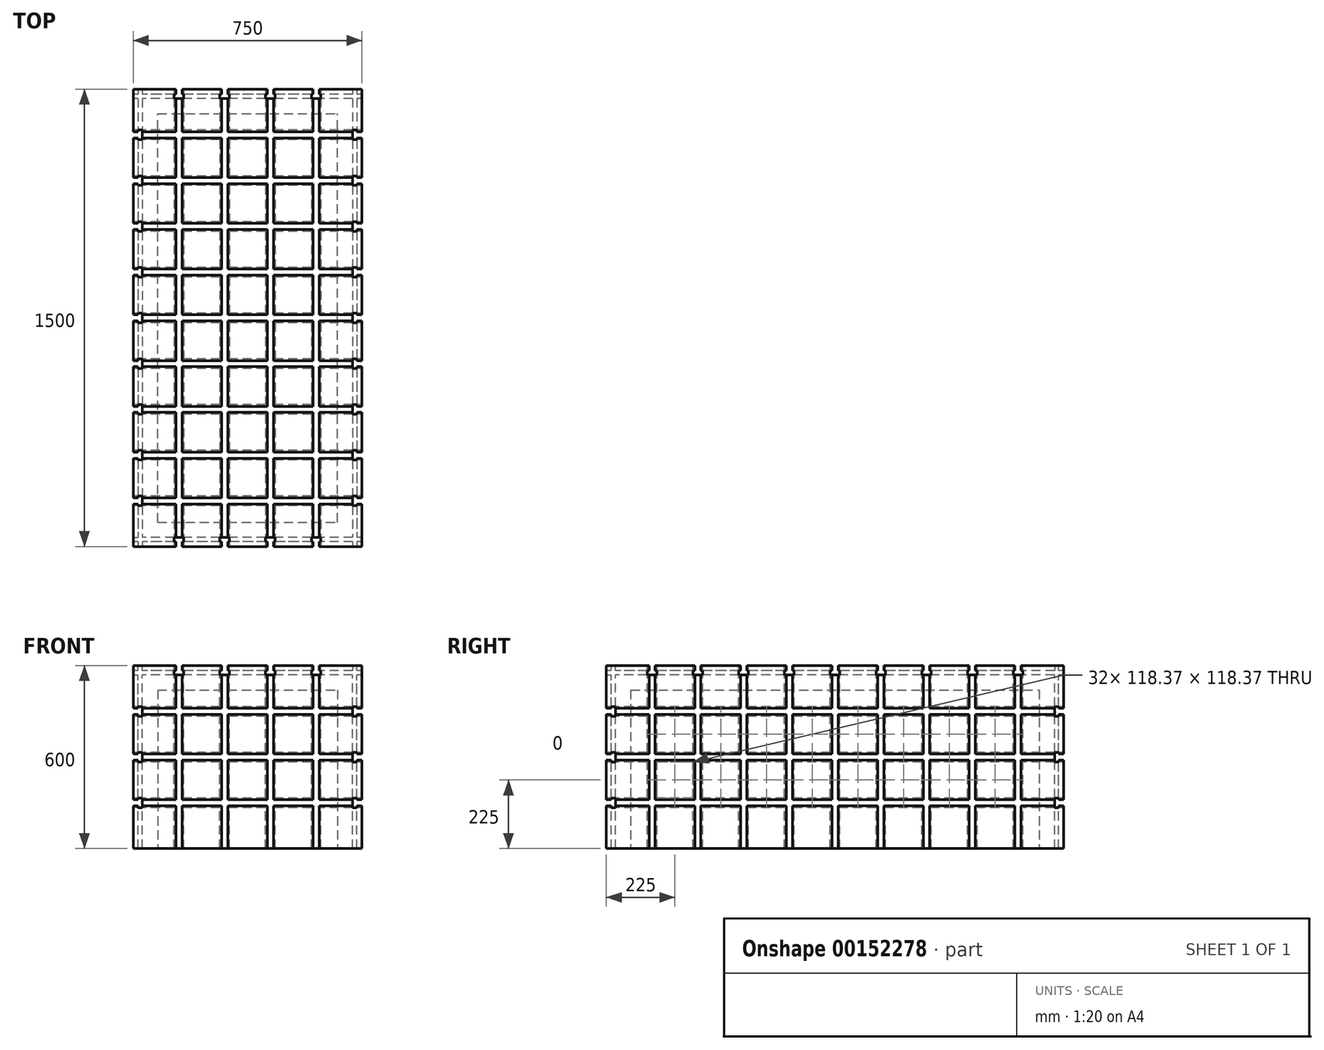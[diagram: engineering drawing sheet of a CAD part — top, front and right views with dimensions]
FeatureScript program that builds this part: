
annotation { "Feature Type Name" : "Feature", "Feature Type Description" : "" }
export const myFeature = defineFeature(function(context is Context, id is Id, definition is map)
    precondition{}
    {
        {
            var Q0;
            Q0=qCreatedBy(makeId("Top.planeOp"),FACE);
            var sketch = newSketch(context, id + "F0", { "sketchPlane" : qUnion([Q0])});
            skLineSegment(sketch, "E0.bottom", {"start": v(-375, 750) * mm, "end": v(375, 750) * mm});
            skLineSegment(sketch, "E0.top", {"start": v(-375, -750) * mm, "end": v(375, -750) * mm});
            skLineSegment(sketch, "E0.left", {"start": v(-375, 750) * mm, "end": v(-375, -750) * mm});
            skLineSegment(sketch, "E0.right", {"start": v(375, 750) * mm, "end": v(375, -750) * mm});
            skPoint(sketch, "E0.middle", {"position": v(0, 0) * mm});
            skSolve(sketch);
        }
        {
            var Q0;
            Q0 = qSketchRegion(id + "F0", true);
            extrude(context, id + "F1", {"entities" : qUnion([Q0]), "oppositeDirection" : true, "depth" : 600 * mm});
        }
        {
            var Q0;
            Q0=makeQuery(id+"F1.opExtrude","SWEPT_FACE",FACE,{"disambiguationData":[OSD([sQuery(id+"F0.wireOp",EDGE,"E0.top")])]});
            var sketch = newSketch(context, id + "F2", { "sketchPlane" : qUnion([Q0])});
            skLineSegment(sketch, "E1", {"start": v(0, 0) * mm, "end": v(0, -600) * mm, "construction": true});
            skLineSegment(sketch, "E2", {"start": v(-375, -300) * mm, "end": v(375, -300) * mm, "construction": true});
            skLineSegment(sketch, "E3", {"start": v(-225, 0) * mm, "end": v(-225, -600) * mm, "construction": true});
            skLineSegment(sketch, "E4", {"start": v(-75, 0) * mm, "end": v(-75, -600) * mm, "construction": true});
            skLineSegment(sketch, "E5.MirrorCS", {"start": v(75, 0) * mm, "end": v(75, -600) * mm, "construction": true});
            skLineSegment(sketch, "E6.MirrorCS", {"start": v(225, 0) * mm, "end": v(225, -600) * mm, "construction": true});
            skLineSegment(sketch, "E7", {"start": v(-375, -150) * mm, "end": v(375, -150) * mm, "construction": true});
            skLineSegment(sketch, "E8.MirrorCS", {"start": v(-375, -450) * mm, "end": v(375, -450) * mm, "construction": true});
            skLineSegment(sketch, "E9", {"start": v(-235, 0) * mm, "end": v(-235, -16.46) * mm});
            skLineSegment(sketch, "E10", {"start": v(-235, -16.46) * mm, "end": v(-240.81, -16.46) * mm});
            skLineSegment(sketch, "E11", {"start": v(-240.81, -16.46) * mm, "end": v(-240.81, -30.16) * mm});
            skLineSegment(sketch, "E12", {"start": v(-240.81, -30.16) * mm, "end": v(-225, -30.16) * mm});
            skLineSegment(sketch, "E13", {"start": v(-235, 0) * mm, "end": v(-235, 10) * mm});
            skLineSegment(sketch, "E14", {"start": v(-235, 10) * mm, "end": v(-225, 10) * mm});
            skLineSegment(sketch, "E15.MirrorCS", {"start": v(-215, -16.46) * mm, "end": v(-209.18, -16.46) * mm});
            skLineSegment(sketch, "E16.MirrorCS", {"start": v(-215, 0) * mm, "end": v(-215, -16.46) * mm});
            skLineSegment(sketch, "E17.MirrorCS", {"start": v(-209.18, -16.46) * mm, "end": v(-209.18, -30.16) * mm});
            skLineSegment(sketch, "E18.MirrorCS", {"start": v(-215, 10) * mm, "end": v(-225, 10) * mm});
            skLineSegment(sketch, "E19.MirrorCS", {"start": v(-209.18, -30.16) * mm, "end": v(-225, -30.16) * mm});
            skLineSegment(sketch, "E20.MirrorCS", {"start": v(-215, 0) * mm, "end": v(-215, 10) * mm});
            skLineSegment(sketch, "E21.1.0.0", {"start": v(-59.18, -16.46) * mm, "end": v(-59.18, -30.16) * mm});
            skLineSegment(sketch, "E21.1.0.1", {"start": v(-59.18, -30.16) * mm, "end": v(-75, -30.16) * mm});
            skLineSegment(sketch, "E21.1.0.2", {"start": v(-85, 0) * mm, "end": v(-85, 10) * mm});
            skLineSegment(sketch, "E21.1.0.3", {"start": v(-65, 0) * mm, "end": v(-65, 10) * mm});
            skLineSegment(sketch, "E21.1.0.4", {"start": v(-65, 10) * mm, "end": v(-75, 10) * mm});
            skLineSegment(sketch, "E21.1.0.5", {"start": v(-90.81, -30.16) * mm, "end": v(-75, -30.16) * mm});
            skLineSegment(sketch, "E21.1.0.6", {"start": v(-90.81, -16.46) * mm, "end": v(-90.81, -30.16) * mm});
            skLineSegment(sketch, "E21.1.0.7", {"start": v(-85, 10) * mm, "end": v(-75, 10) * mm});
            skLineSegment(sketch, "E21.1.0.8", {"start": v(-85, 0) * mm, "end": v(-85, -16.46) * mm});
            skLineSegment(sketch, "E21.1.0.9", {"start": v(-65, 0) * mm, "end": v(-65, -16.46) * mm});
            skLineSegment(sketch, "E21.1.0.10", {"start": v(-85, -16.46) * mm, "end": v(-90.81, -16.46) * mm});
            skLineSegment(sketch, "E21.1.0.11", {"start": v(-65, -16.46) * mm, "end": v(-59.18, -16.46) * mm});
            skLineSegment(sketch, "E21.2.0.0", {"start": v(90.82, -16.46) * mm, "end": v(90.82, -30.16) * mm});
            skLineSegment(sketch, "E21.2.0.1", {"start": v(90.82, -30.16) * mm, "end": v(75, -30.16) * mm});
            skLineSegment(sketch, "E21.2.0.2", {"start": v(65, 0) * mm, "end": v(65, 10) * mm});
            skLineSegment(sketch, "E21.2.0.3", {"start": v(85, 0) * mm, "end": v(85, 10) * mm});
            skLineSegment(sketch, "E21.2.0.4", {"start": v(85, 10) * mm, "end": v(75, 10) * mm});
            skLineSegment(sketch, "E21.2.0.5", {"start": v(59.19, -30.16) * mm, "end": v(75, -30.16) * mm});
            skLineSegment(sketch, "E21.2.0.6", {"start": v(59.19, -16.46) * mm, "end": v(59.19, -30.16) * mm});
            skLineSegment(sketch, "E21.2.0.7", {"start": v(65, 10) * mm, "end": v(75, 10) * mm});
            skLineSegment(sketch, "E21.2.0.8", {"start": v(65, 0) * mm, "end": v(65, -16.46) * mm});
            skLineSegment(sketch, "E21.2.0.9", {"start": v(85, 0) * mm, "end": v(85, -16.46) * mm});
            skLineSegment(sketch, "E21.2.0.10", {"start": v(65, -16.46) * mm, "end": v(59.19, -16.46) * mm});
            skLineSegment(sketch, "E21.2.0.11", {"start": v(85, -16.46) * mm, "end": v(90.82, -16.46) * mm});
            skLineSegment(sketch, "E21.3.0.0", {"start": v(240.82, -16.46) * mm, "end": v(240.82, -30.16) * mm});
            skLineSegment(sketch, "E21.3.0.1", {"start": v(240.82, -30.16) * mm, "end": v(225, -30.16) * mm});
            skLineSegment(sketch, "E21.3.0.2", {"start": v(215, 0) * mm, "end": v(215, 10) * mm});
            skLineSegment(sketch, "E21.3.0.3", {"start": v(235, 0) * mm, "end": v(235, 10) * mm});
            skLineSegment(sketch, "E21.3.0.4", {"start": v(235, 10) * mm, "end": v(225, 10) * mm});
            skLineSegment(sketch, "E21.3.0.5", {"start": v(209.19, -30.16) * mm, "end": v(225, -30.16) * mm});
            skLineSegment(sketch, "E21.3.0.6", {"start": v(209.19, -16.46) * mm, "end": v(209.19, -30.16) * mm});
            skLineSegment(sketch, "E21.3.0.7", {"start": v(215, 10) * mm, "end": v(225, 10) * mm});
            skLineSegment(sketch, "E21.3.0.8", {"start": v(215, 0) * mm, "end": v(215, -16.46) * mm});
            skLineSegment(sketch, "E21.3.0.9", {"start": v(235, 0) * mm, "end": v(235, -16.46) * mm});
            skLineSegment(sketch, "E21.3.0.10", {"start": v(215, -16.46) * mm, "end": v(209.19, -16.46) * mm});
            skLineSegment(sketch, "E21.3.0.11", {"start": v(235, -16.46) * mm, "end": v(240.81, -16.46) * mm});
            skLineSegment(sketch, "E21.direction1", {"start": v(-240.81, -30.16) * mm, "end": v(-90.81, -30.16) * mm, "construction": true});
            skLineSegment(sketch, "E22", {"start": v(-375, -160) * mm, "end": v(-358.54, -160) * mm});
            skLineSegment(sketch, "E23", {"start": v(-358.54, -160) * mm, "end": v(-358.54, -165.82) * mm});
            skLineSegment(sketch, "E24", {"start": v(-358.54, -165.82) * mm, "end": v(-344.84, -165.82) * mm});
            skLineSegment(sketch, "E25", {"start": v(-344.84, -165.82) * mm, "end": v(-344.84, -150) * mm});
            skLineSegment(sketch, "E26", {"start": v(-375, -160) * mm, "end": v(-385, -160) * mm});
            skLineSegment(sketch, "E27", {"start": v(-385, -160) * mm, "end": v(-385, -150) * mm});
            skLineSegment(sketch, "E28.MirrorCS", {"start": v(-358.54, -134.18) * mm, "end": v(-344.84, -134.18) * mm});
            skLineSegment(sketch, "E29.MirrorCS", {"start": v(-358.54, -140) * mm, "end": v(-358.54, -134.18) * mm});
            skLineSegment(sketch, "E30.MirrorCS", {"start": v(-375, -140) * mm, "end": v(-358.54, -140) * mm});
            skLineSegment(sketch, "E31.MirrorCS", {"start": v(-344.84, -134.18) * mm, "end": v(-344.84, -150) * mm});
            skLineSegment(sketch, "E32.MirrorCS", {"start": v(-375, -140) * mm, "end": v(-385, -140) * mm});
            skLineSegment(sketch, "E33.MirrorCS", {"start": v(-385, -140) * mm, "end": v(-385, -150) * mm});
            skLineSegment(sketch, "E34.0.1.0", {"start": v(-375, -310) * mm, "end": v(-358.54, -310) * mm});
            skLineSegment(sketch, "E34.0.1.1", {"start": v(-375, -290) * mm, "end": v(-358.54, -290) * mm});
            skLineSegment(sketch, "E34.0.1.2", {"start": v(-344.84, -284.18) * mm, "end": v(-344.84, -300) * mm});
            skLineSegment(sketch, "E34.0.1.3", {"start": v(-358.54, -290) * mm, "end": v(-358.54, -284.18) * mm});
            skLineSegment(sketch, "E34.0.1.4", {"start": v(-358.54, -284.18) * mm, "end": v(-344.84, -284.18) * mm});
            skLineSegment(sketch, "E34.0.1.5", {"start": v(-385, -310) * mm, "end": v(-385, -300) * mm});
            skLineSegment(sketch, "E34.0.1.6", {"start": v(-344.84, -315.82) * mm, "end": v(-344.84, -300) * mm});
            skLineSegment(sketch, "E34.0.1.7", {"start": v(-375, -310) * mm, "end": v(-385, -310) * mm});
            skLineSegment(sketch, "E34.0.1.8", {"start": v(-385, -290) * mm, "end": v(-385, -300) * mm});
            skLineSegment(sketch, "E34.0.1.9", {"start": v(-358.54, -315.82) * mm, "end": v(-344.84, -315.82) * mm});
            skLineSegment(sketch, "E34.0.1.10", {"start": v(-375, -290) * mm, "end": v(-385, -290) * mm});
            skLineSegment(sketch, "E34.0.1.11", {"start": v(-358.54, -310) * mm, "end": v(-358.54, -315.82) * mm});
            skLineSegment(sketch, "E34.0.2.0", {"start": v(-375, -460) * mm, "end": v(-358.54, -460) * mm});
            skLineSegment(sketch, "E34.0.2.1", {"start": v(-375, -440) * mm, "end": v(-358.54, -440) * mm});
            skLineSegment(sketch, "E34.0.2.2", {"start": v(-344.84, -434.18) * mm, "end": v(-344.84, -450) * mm});
            skLineSegment(sketch, "E34.0.2.3", {"start": v(-358.54, -440) * mm, "end": v(-358.54, -434.18) * mm});
            skLineSegment(sketch, "E34.0.2.4", {"start": v(-358.54, -434.19) * mm, "end": v(-344.84, -434.19) * mm});
            skLineSegment(sketch, "E34.0.2.5", {"start": v(-385, -460) * mm, "end": v(-385, -450) * mm});
            skLineSegment(sketch, "E34.0.2.6", {"start": v(-344.84, -465.82) * mm, "end": v(-344.84, -450) * mm});
            skLineSegment(sketch, "E34.0.2.7", {"start": v(-375, -460) * mm, "end": v(-385, -460) * mm});
            skLineSegment(sketch, "E34.0.2.8", {"start": v(-385, -440) * mm, "end": v(-385, -450) * mm});
            skLineSegment(sketch, "E34.0.2.9", {"start": v(-358.54, -465.82) * mm, "end": v(-344.84, -465.82) * mm});
            skLineSegment(sketch, "E34.0.2.10", {"start": v(-375, -440) * mm, "end": v(-385, -440) * mm});
            skLineSegment(sketch, "E34.0.2.11", {"start": v(-358.54, -460) * mm, "end": v(-358.54, -465.82) * mm});
            skLineSegment(sketch, "E34.direction1", {"start": v(-3796.34, -160) * mm, "end": v(-385, -160) * mm, "construction": true});
            skLineSegment(sketch, "E34.direction2", {"start": v(-385, -160) * mm, "end": v(-385, -310) * mm, "construction": true});
            skLineSegment(sketch, "E35.MirrorCS", {"start": v(3796.34, -160) * mm, "end": v(385, -160) * mm, "construction": true});
            skLineSegment(sketch, "E36.MirrorCS", {"start": v(375, -160) * mm, "end": v(385, -160) * mm});
            skLineSegment(sketch, "E37.MirrorCS", {"start": v(385, -160) * mm, "end": v(385, -150) * mm});
            skLineSegment(sketch, "E38.MirrorCS", {"start": v(385, -310) * mm, "end": v(385, -300) * mm});
            skLineSegment(sketch, "E39.MirrorCS", {"start": v(385, -290) * mm, "end": v(385, -300) * mm});
            skLineSegment(sketch, "E40.MirrorCS", {"start": v(358.54, -440) * mm, "end": v(358.54, -434.18) * mm});
            skLineSegment(sketch, "E41.MirrorCS", {"start": v(375, -310) * mm, "end": v(385, -310) * mm});
            skLineSegment(sketch, "E42.MirrorCS", {"start": v(375, -290) * mm, "end": v(385, -290) * mm});
            skLineSegment(sketch, "E43.MirrorCS", {"start": v(375, -140) * mm, "end": v(385, -140) * mm});
            skLineSegment(sketch, "E44.MirrorCS", {"start": v(358.54, -160) * mm, "end": v(358.54, -165.82) * mm});
            skLineSegment(sketch, "E45.MirrorCS", {"start": v(375, -440) * mm, "end": v(358.54, -440) * mm});
            skLineSegment(sketch, "E46.MirrorCS", {"start": v(385, -440) * mm, "end": v(385, -450) * mm});
            skLineSegment(sketch, "E47.MirrorCS", {"start": v(358.54, -165.82) * mm, "end": v(344.84, -165.82) * mm});
            skLineSegment(sketch, "E48.MirrorCS", {"start": v(375, -440) * mm, "end": v(385, -440) * mm});
            skLineSegment(sketch, "E49.MirrorCS", {"start": v(385, -140) * mm, "end": v(385, -150) * mm});
            skLineSegment(sketch, "E50.MirrorCS", {"start": v(375, -160) * mm, "end": v(358.54, -160) * mm});
            skLineSegment(sketch, "E51.MirrorCS", {"start": v(358.54, -434.19) * mm, "end": v(344.84, -434.19) * mm});
            skLineSegment(sketch, "E52.MirrorCS", {"start": v(344.84, -165.82) * mm, "end": v(344.84, -150) * mm});
            skLineSegment(sketch, "E53.MirrorCS", {"start": v(375, -290) * mm, "end": v(358.54, -290) * mm});
            skLineSegment(sketch, "E54.MirrorCS", {"start": v(358.54, -460) * mm, "end": v(358.54, -465.82) * mm});
            skLineSegment(sketch, "E55.MirrorCS", {"start": v(344.84, -434.18) * mm, "end": v(344.84, -450) * mm});
            skLineSegment(sketch, "E56.MirrorCS", {"start": v(358.54, -465.82) * mm, "end": v(344.84, -465.82) * mm});
            skLineSegment(sketch, "E57.MirrorCS", {"start": v(344.84, -134.18) * mm, "end": v(344.84, -150) * mm});
            skLineSegment(sketch, "E58.MirrorCS", {"start": v(344.84, -315.82) * mm, "end": v(344.84, -300) * mm});
            skLineSegment(sketch, "E59.MirrorCS", {"start": v(358.54, -284.18) * mm, "end": v(344.84, -284.18) * mm});
            skLineSegment(sketch, "E60.MirrorCS", {"start": v(375, -140) * mm, "end": v(358.54, -140) * mm});
            skLineSegment(sketch, "E61.MirrorCS", {"start": v(375, -460) * mm, "end": v(358.54, -460) * mm});
            skLineSegment(sketch, "E62.MirrorCS", {"start": v(375, -460) * mm, "end": v(385, -460) * mm});
            skLineSegment(sketch, "E63.MirrorCS", {"start": v(358.54, -290) * mm, "end": v(358.54, -284.18) * mm});
            skLineSegment(sketch, "E64.MirrorCS", {"start": v(344.84, -465.82) * mm, "end": v(344.84, -450) * mm});
            skLineSegment(sketch, "E65.MirrorCS", {"start": v(344.84, -284.18) * mm, "end": v(344.84, -300) * mm});
            skLineSegment(sketch, "E66.MirrorCS", {"start": v(375, -310) * mm, "end": v(358.54, -310) * mm});
            skLineSegment(sketch, "E67.MirrorCS", {"start": v(358.54, -310) * mm, "end": v(358.54, -315.82) * mm});
            skLineSegment(sketch, "E68.MirrorCS", {"start": v(385, -460) * mm, "end": v(385, -450) * mm});
            skLineSegment(sketch, "E69.MirrorCS", {"start": v(358.54, -134.18) * mm, "end": v(344.84, -134.18) * mm});
            skLineSegment(sketch, "E70.MirrorCS", {"start": v(358.54, -140) * mm, "end": v(358.54, -134.18) * mm});
            skLineSegment(sketch, "E71.MirrorCS", {"start": v(358.54, -315.82) * mm, "end": v(344.84, -315.82) * mm});
            skLineSegment(sketch, "E72.MirrorCS", {"start": v(385, -160) * mm, "end": v(385, -310) * mm, "construction": true});
            skSolve(sketch);
        }
        {
            var Q0;
            Q0 = qSketchRegion(id + "F2", true);
            extrude(context, id + "F3", {"entities" : qUnion([Q0]), "operationType" : NewBodyOperationType.REMOVE, "endBound" : BoundingType.THROUGH_ALL, "oppositeDirection" : true, "depth" : 25 * mm});
        }
        {
            var Q0;
            {var subQ1=sQuery(id+"F0.wireOp",EDGE,"E0.left");Q0=makeQuery(id+"F3.boolean.opBoolean","SPLIT",FACE,{"disambiguationData":[TD([makeQuery(id+"F3.opExtrude","SWEPT_FACE",FACE,{"disambiguationData":[OSD([sQuery(id+"F2.wireOp",EDGE,"E34.0.2.0"),sQuery(id+"F2.wireOp",EDGE,"E34.0.2.7")])]})])],"derivedFrom":makeQuery(id+"F1.opExtrude","SWEPT_FACE",FACE,{"disambiguationData":[OSD([subQ1])]})});}
            var sketch = newSketch(context, id + "F4", { "sketchPlane" : qUnion([Q0])});
            skLineSegment(sketch, "E73", {"start": v(-600, 0) * mm, "end": v(-600, -600) * mm, "construction": true});
            skLineSegment(sketch, "E74.1.0.0", {"start": v(-450, 0) * mm, "end": v(-450, -600) * mm, "construction": true});
            skLineSegment(sketch, "E74.2.0.0", {"start": v(-300, 0) * mm, "end": v(-300, -600) * mm, "construction": true});
            skLineSegment(sketch, "E74.3.0.0", {"start": v(-150, 0) * mm, "end": v(-150, -600) * mm, "construction": true});
            skLineSegment(sketch, "E74.4.0.0", {"start": v(0, 0) * mm, "end": v(0, -600) * mm, "construction": true});
            skLineSegment(sketch, "E74.5.0.0", {"start": v(150, 0) * mm, "end": v(150, -600) * mm, "construction": true});
            skLineSegment(sketch, "E74.6.0.0", {"start": v(300, 0) * mm, "end": v(300, -600) * mm, "construction": true});
            skLineSegment(sketch, "E74.7.0.0", {"start": v(450, 0) * mm, "end": v(450, -600) * mm, "construction": true});
            skLineSegment(sketch, "E74.8.0.0", {"start": v(600, 0) * mm, "end": v(600, -600) * mm, "construction": true});
            skLineSegment(sketch, "E74.direction1", {"start": v(-600, -600) * mm, "end": v(-450, -600) * mm, "construction": true});
            skLineSegment(sketch, "E75", {"start": v(-750, -450) * mm, "end": v(750, -450) * mm, "construction": true});
            skLineSegment(sketch, "E76", {"start": v(-610, 0) * mm, "end": v(-610, -16.46) * mm});
            skLineSegment(sketch, "E77", {"start": v(-610, -16.46) * mm, "end": v(-615.81, -16.46) * mm});
            skLineSegment(sketch, "E78", {"start": v(-615.81, -16.46) * mm, "end": v(-615.81, -30.16) * mm});
            skLineSegment(sketch, "E79", {"start": v(-615.81, -30.16) * mm, "end": v(-600, -30.16) * mm});
            skLineSegment(sketch, "E80", {"start": v(-610, 0) * mm, "end": v(-610, 49.87) * mm});
            skLineSegment(sketch, "E81", {"start": v(-610, 49.87) * mm, "end": v(-600, 49.87) * mm});
            skLineSegment(sketch, "E82.MirrorCS", {"start": v(-590, -16.46) * mm, "end": v(-584.18, -16.46) * mm});
            skLineSegment(sketch, "E83.MirrorCS", {"start": v(-590, 0) * mm, "end": v(-590, -16.46) * mm});
            skLineSegment(sketch, "E84.MirrorCS", {"start": v(-584.18, -16.46) * mm, "end": v(-584.18, -30.16) * mm});
            skLineSegment(sketch, "E85.MirrorCS", {"start": v(-584.18, -30.16) * mm, "end": v(-600, -30.16) * mm});
            skLineSegment(sketch, "E86.MirrorCS", {"start": v(-590, 0) * mm, "end": v(-590, 49.87) * mm});
            skLineSegment(sketch, "E87.MirrorCS", {"start": v(-590, 49.87) * mm, "end": v(-600, 49.87) * mm});
            skLineSegment(sketch, "E88.1.0.0", {"start": v(-434.18, -30.16) * mm, "end": v(-450, -30.16) * mm});
            skLineSegment(sketch, "E88.1.0.1", {"start": v(-440, 49.87) * mm, "end": v(-450, 49.87) * mm});
            skLineSegment(sketch, "E88.1.0.2", {"start": v(-465.81, -30.16) * mm, "end": v(-450, -30.16) * mm});
            skLineSegment(sketch, "E88.1.0.3", {"start": v(-460, 49.87) * mm, "end": v(-450, 49.87) * mm});
            skLineSegment(sketch, "E88.1.0.4", {"start": v(-440, 0) * mm, "end": v(-440, -16.46) * mm});
            skLineSegment(sketch, "E88.1.0.5", {"start": v(-434.18, -16.46) * mm, "end": v(-434.18, -30.16) * mm});
            skLineSegment(sketch, "E88.1.0.6", {"start": v(-460, 0) * mm, "end": v(-460, -16.46) * mm});
            skLineSegment(sketch, "E88.1.0.7", {"start": v(-465.81, -16.46) * mm, "end": v(-465.81, -30.16) * mm});
            skLineSegment(sketch, "E88.1.0.8", {"start": v(-440, 0) * mm, "end": v(-440, 49.87) * mm});
            skLineSegment(sketch, "E88.1.0.9", {"start": v(-460, -16.46) * mm, "end": v(-465.81, -16.46) * mm});
            skLineSegment(sketch, "E88.1.0.10", {"start": v(-440, -16.46) * mm, "end": v(-434.18, -16.46) * mm});
            skLineSegment(sketch, "E88.1.0.11", {"start": v(-460, 0) * mm, "end": v(-460, 49.87) * mm});
            skLineSegment(sketch, "E88.2.0.0", {"start": v(-284.18, -30.16) * mm, "end": v(-300, -30.16) * mm});
            skLineSegment(sketch, "E88.2.0.1", {"start": v(-290, 49.87) * mm, "end": v(-300, 49.87) * mm});
            skLineSegment(sketch, "E88.2.0.2", {"start": v(-315.81, -30.16) * mm, "end": v(-300, -30.16) * mm});
            skLineSegment(sketch, "E88.2.0.3", {"start": v(-310, 49.87) * mm, "end": v(-300, 49.87) * mm});
            skLineSegment(sketch, "E88.2.0.4", {"start": v(-290, 0) * mm, "end": v(-290, -16.46) * mm});
            skLineSegment(sketch, "E88.2.0.5", {"start": v(-284.18, -16.46) * mm, "end": v(-284.18, -30.16) * mm});
            skLineSegment(sketch, "E88.2.0.6", {"start": v(-310, 0) * mm, "end": v(-310, -16.46) * mm});
            skLineSegment(sketch, "E88.2.0.7", {"start": v(-315.81, -16.46) * mm, "end": v(-315.81, -30.16) * mm});
            skLineSegment(sketch, "E88.2.0.8", {"start": v(-290, 0) * mm, "end": v(-290, 49.87) * mm});
            skLineSegment(sketch, "E88.2.0.9", {"start": v(-310, -16.46) * mm, "end": v(-315.81, -16.46) * mm});
            skLineSegment(sketch, "E88.2.0.10", {"start": v(-290, -16.46) * mm, "end": v(-284.18, -16.46) * mm});
            skLineSegment(sketch, "E88.2.0.11", {"start": v(-310, 0) * mm, "end": v(-310, 49.87) * mm});
            skLineSegment(sketch, "E88.3.0.0", {"start": v(-134.18, -30.16) * mm, "end": v(-150, -30.16) * mm});
            skLineSegment(sketch, "E88.3.0.1", {"start": v(-140, 49.87) * mm, "end": v(-150, 49.87) * mm});
            skLineSegment(sketch, "E88.3.0.2", {"start": v(-165.81, -30.16) * mm, "end": v(-150, -30.16) * mm});
            skLineSegment(sketch, "E88.3.0.3", {"start": v(-160, 49.87) * mm, "end": v(-150, 49.87) * mm});
            skLineSegment(sketch, "E88.3.0.4", {"start": v(-140, 0) * mm, "end": v(-140, -16.46) * mm});
            skLineSegment(sketch, "E88.3.0.5", {"start": v(-134.18, -16.46) * mm, "end": v(-134.18, -30.16) * mm});
            skLineSegment(sketch, "E88.3.0.6", {"start": v(-160, 0) * mm, "end": v(-160, -16.46) * mm});
            skLineSegment(sketch, "E88.3.0.7", {"start": v(-165.81, -16.46) * mm, "end": v(-165.81, -30.16) * mm});
            skLineSegment(sketch, "E88.3.0.8", {"start": v(-140, 0) * mm, "end": v(-140, 49.87) * mm});
            skLineSegment(sketch, "E88.3.0.9", {"start": v(-160, -16.46) * mm, "end": v(-165.81, -16.46) * mm});
            skLineSegment(sketch, "E88.3.0.10", {"start": v(-140, -16.46) * mm, "end": v(-134.18, -16.46) * mm});
            skLineSegment(sketch, "E88.3.0.11", {"start": v(-160, 0) * mm, "end": v(-160, 49.87) * mm});
            skLineSegment(sketch, "E88.4.0.0", {"start": v(15.82, -30.16) * mm, "end": v(0, -30.16) * mm});
            skLineSegment(sketch, "E88.4.0.1", {"start": v(10, 49.87) * mm, "end": v(0, 49.87) * mm});
            skLineSegment(sketch, "E88.4.0.2", {"start": v(-15.81, -30.16) * mm, "end": v(0, -30.16) * mm});
            skLineSegment(sketch, "E88.4.0.3", {"start": v(-10, 49.87) * mm, "end": v(0, 49.87) * mm});
            skLineSegment(sketch, "E88.4.0.4", {"start": v(10, 0) * mm, "end": v(10, -16.46) * mm});
            skLineSegment(sketch, "E88.4.0.5", {"start": v(15.82, -16.46) * mm, "end": v(15.82, -30.16) * mm});
            skLineSegment(sketch, "E88.4.0.6", {"start": v(-10, 0) * mm, "end": v(-10, -16.46) * mm});
            skLineSegment(sketch, "E88.4.0.7", {"start": v(-15.81, -16.46) * mm, "end": v(-15.81, -30.16) * mm});
            skLineSegment(sketch, "E88.4.0.8", {"start": v(10, 0) * mm, "end": v(10, 49.87) * mm});
            skLineSegment(sketch, "E88.4.0.9", {"start": v(-10, -16.46) * mm, "end": v(-15.81, -16.46) * mm});
            skLineSegment(sketch, "E88.4.0.10", {"start": v(10, -16.46) * mm, "end": v(15.82, -16.46) * mm});
            skLineSegment(sketch, "E88.4.0.11", {"start": v(-10, 0) * mm, "end": v(-10, 49.87) * mm});
            skLineSegment(sketch, "E88.5.0.0", {"start": v(165.82, -30.16) * mm, "end": v(150, -30.16) * mm});
            skLineSegment(sketch, "E88.5.0.1", {"start": v(160, 49.87) * mm, "end": v(150, 49.87) * mm});
            skLineSegment(sketch, "E88.5.0.2", {"start": v(134.19, -30.16) * mm, "end": v(150, -30.16) * mm});
            skLineSegment(sketch, "E88.5.0.3", {"start": v(140, 49.87) * mm, "end": v(150, 49.87) * mm});
            skLineSegment(sketch, "E88.5.0.4", {"start": v(160, 0) * mm, "end": v(160, -16.46) * mm});
            skLineSegment(sketch, "E88.5.0.5", {"start": v(165.82, -16.46) * mm, "end": v(165.82, -30.16) * mm});
            skLineSegment(sketch, "E88.5.0.6", {"start": v(140, 0) * mm, "end": v(140, -16.46) * mm});
            skLineSegment(sketch, "E88.5.0.7", {"start": v(134.19, -16.46) * mm, "end": v(134.19, -30.16) * mm});
            skLineSegment(sketch, "E88.5.0.8", {"start": v(160, 0) * mm, "end": v(160, 49.87) * mm});
            skLineSegment(sketch, "E88.5.0.9", {"start": v(140, -16.46) * mm, "end": v(134.19, -16.46) * mm});
            skLineSegment(sketch, "E88.5.0.10", {"start": v(160, -16.46) * mm, "end": v(165.82, -16.46) * mm});
            skLineSegment(sketch, "E88.5.0.11", {"start": v(140, 0) * mm, "end": v(140, 49.87) * mm});
            skLineSegment(sketch, "E88.6.0.0", {"start": v(315.82, -30.16) * mm, "end": v(300, -30.16) * mm});
            skLineSegment(sketch, "E88.6.0.1", {"start": v(310, 49.87) * mm, "end": v(300, 49.87) * mm});
            skLineSegment(sketch, "E88.6.0.2", {"start": v(284.19, -30.16) * mm, "end": v(300, -30.16) * mm});
            skLineSegment(sketch, "E88.6.0.3", {"start": v(290, 49.87) * mm, "end": v(300, 49.87) * mm});
            skLineSegment(sketch, "E88.6.0.4", {"start": v(310, 0) * mm, "end": v(310, -16.46) * mm});
            skLineSegment(sketch, "E88.6.0.5", {"start": v(315.82, -16.46) * mm, "end": v(315.82, -30.16) * mm});
            skLineSegment(sketch, "E88.6.0.6", {"start": v(290, 0) * mm, "end": v(290, -16.46) * mm});
            skLineSegment(sketch, "E88.6.0.7", {"start": v(284.19, -16.46) * mm, "end": v(284.19, -30.16) * mm});
            skLineSegment(sketch, "E88.6.0.8", {"start": v(310, 0) * mm, "end": v(310, 49.87) * mm});
            skLineSegment(sketch, "E88.6.0.9", {"start": v(290, -16.46) * mm, "end": v(284.19, -16.46) * mm});
            skLineSegment(sketch, "E88.6.0.10", {"start": v(310, -16.46) * mm, "end": v(315.82, -16.46) * mm});
            skLineSegment(sketch, "E88.6.0.11", {"start": v(290, 0) * mm, "end": v(290, 49.87) * mm});
            skLineSegment(sketch, "E88.7.0.0", {"start": v(465.82, -30.16) * mm, "end": v(450, -30.16) * mm});
            skLineSegment(sketch, "E88.7.0.1", {"start": v(460, 49.87) * mm, "end": v(450, 49.87) * mm});
            skLineSegment(sketch, "E88.7.0.2", {"start": v(434.19, -30.16) * mm, "end": v(450, -30.16) * mm});
            skLineSegment(sketch, "E88.7.0.3", {"start": v(440, 49.87) * mm, "end": v(450, 49.87) * mm});
            skLineSegment(sketch, "E88.7.0.4", {"start": v(460, 0) * mm, "end": v(460, -16.46) * mm});
            skLineSegment(sketch, "E88.7.0.5", {"start": v(465.82, -16.46) * mm, "end": v(465.82, -30.16) * mm});
            skLineSegment(sketch, "E88.7.0.6", {"start": v(440, 0) * mm, "end": v(440, -16.46) * mm});
            skLineSegment(sketch, "E88.7.0.7", {"start": v(434.19, -16.46) * mm, "end": v(434.19, -30.16) * mm});
            skLineSegment(sketch, "E88.7.0.8", {"start": v(460, 0) * mm, "end": v(460, 49.87) * mm});
            skLineSegment(sketch, "E88.7.0.9", {"start": v(440, -16.46) * mm, "end": v(434.19, -16.46) * mm});
            skLineSegment(sketch, "E88.7.0.10", {"start": v(460, -16.46) * mm, "end": v(465.82, -16.46) * mm});
            skLineSegment(sketch, "E88.7.0.11", {"start": v(440, 0) * mm, "end": v(440, 49.87) * mm});
            skLineSegment(sketch, "E88.8.0.0", {"start": v(615.82, -30.16) * mm, "end": v(600, -30.16) * mm});
            skLineSegment(sketch, "E88.8.0.1", {"start": v(610, 49.87) * mm, "end": v(600, 49.87) * mm});
            skLineSegment(sketch, "E88.8.0.2", {"start": v(584.19, -30.16) * mm, "end": v(600, -30.16) * mm});
            skLineSegment(sketch, "E88.8.0.3", {"start": v(590, 49.87) * mm, "end": v(600, 49.87) * mm});
            skLineSegment(sketch, "E88.8.0.4", {"start": v(610, 0) * mm, "end": v(610, -16.46) * mm});
            skLineSegment(sketch, "E88.8.0.5", {"start": v(615.82, -16.46) * mm, "end": v(615.82, -30.16) * mm});
            skLineSegment(sketch, "E88.8.0.6", {"start": v(590, 0) * mm, "end": v(590, -16.46) * mm});
            skLineSegment(sketch, "E88.8.0.7", {"start": v(584.19, -16.46) * mm, "end": v(584.19, -30.16) * mm});
            skLineSegment(sketch, "E88.8.0.8", {"start": v(610, 0) * mm, "end": v(610, 49.87) * mm});
            skLineSegment(sketch, "E88.8.0.9", {"start": v(590, -16.46) * mm, "end": v(584.19, -16.46) * mm});
            skLineSegment(sketch, "E88.8.0.10", {"start": v(610, -16.46) * mm, "end": v(615.82, -16.46) * mm});
            skLineSegment(sketch, "E88.8.0.11", {"start": v(590, 0) * mm, "end": v(590, 49.87) * mm});
            skLineSegment(sketch, "E88.direction1", {"start": v(-615.81, -30.16) * mm, "end": v(-465.81, -30.16) * mm, "construction": true});
            skLineSegment(sketch, "E89.0.1.0", {"start": v(-750, -300) * mm, "end": v(750, -300) * mm, "construction": true});
            skLineSegment(sketch, "E89.0.2.0", {"start": v(-750, -150) * mm, "end": v(750, -150) * mm, "construction": true});
            skLineSegment(sketch, "E89.direction1", {"start": v(-750, -450) * mm, "end": v(-725, -450) * mm, "construction": true});
            skLineSegment(sketch, "E89.direction2", {"start": v(-750, -450) * mm, "end": v(-750, -300) * mm, "construction": true});
            skLineSegment(sketch, "E90", {"start": v(-750, -160) * mm, "end": v(-733.54, -160) * mm});
            skLineSegment(sketch, "E91", {"start": v(-733.54, -160) * mm, "end": v(-733.54, -165.82) * mm});
            skLineSegment(sketch, "E92", {"start": v(-733.54, -165.82) * mm, "end": v(-719.84, -165.82) * mm});
            skLineSegment(sketch, "E93", {"start": v(-719.84, -165.82) * mm, "end": v(-719.84, -150) * mm});
            skLineSegment(sketch, "E94", {"start": v(-750, -160) * mm, "end": v(-766.31, -160) * mm});
            skLineSegment(sketch, "E95", {"start": v(-766.31, -160) * mm, "end": v(-766.31, -150) * mm});
            skLineSegment(sketch, "E96.MirrorCS", {"start": v(-733.54, -140) * mm, "end": v(-733.54, -134.18) * mm});
            skLineSegment(sketch, "E97.MirrorCS", {"start": v(-766.31, -140) * mm, "end": v(-766.31, -150) * mm});
            skLineSegment(sketch, "E98.MirrorCS", {"start": v(-750, -140) * mm, "end": v(-766.31, -140) * mm});
            skLineSegment(sketch, "E99.MirrorCS", {"start": v(-733.54, -134.18) * mm, "end": v(-719.84, -134.18) * mm});
            skLineSegment(sketch, "E100.MirrorCS", {"start": v(-719.84, -134.18) * mm, "end": v(-719.84, -150) * mm});
            skLineSegment(sketch, "E101.MirrorCS", {"start": v(-750, -140) * mm, "end": v(-733.54, -140) * mm});
            skLineSegment(sketch, "E102.0.1.0", {"start": v(-719.84, -284.18) * mm, "end": v(-719.84, -300) * mm});
            skLineSegment(sketch, "E102.0.1.1", {"start": v(-766.31, -290) * mm, "end": v(-766.31, -300) * mm});
            skLineSegment(sketch, "E102.0.1.2", {"start": v(-733.54, -315.81) * mm, "end": v(-719.84, -315.81) * mm});
            skLineSegment(sketch, "E102.0.1.3", {"start": v(-750, -290) * mm, "end": v(-766.31, -290) * mm});
            skLineSegment(sketch, "E102.0.1.4", {"start": v(-750, -310) * mm, "end": v(-766.31, -310) * mm});
            skLineSegment(sketch, "E102.0.1.5", {"start": v(-733.54, -284.18) * mm, "end": v(-719.84, -284.18) * mm});
            skLineSegment(sketch, "E102.0.1.6", {"start": v(-766.31, -310) * mm, "end": v(-766.31, -300) * mm});
            skLineSegment(sketch, "E102.0.1.7", {"start": v(-750, -310) * mm, "end": v(-733.54, -310) * mm});
            skLineSegment(sketch, "E102.0.1.8", {"start": v(-719.84, -315.81) * mm, "end": v(-719.84, -300) * mm});
            skLineSegment(sketch, "E102.0.1.9", {"start": v(-750, -290) * mm, "end": v(-733.54, -290) * mm});
            skLineSegment(sketch, "E102.0.1.10", {"start": v(-733.54, -290) * mm, "end": v(-733.54, -284.18) * mm});
            skLineSegment(sketch, "E102.0.1.11", {"start": v(-733.54, -310) * mm, "end": v(-733.54, -315.81) * mm});
            skLineSegment(sketch, "E102.0.2.0", {"start": v(-719.84, -434.19) * mm, "end": v(-719.84, -450) * mm});
            skLineSegment(sketch, "E102.0.2.1", {"start": v(-766.31, -440) * mm, "end": v(-766.31, -450) * mm});
            skLineSegment(sketch, "E102.0.2.2", {"start": v(-733.54, -465.81) * mm, "end": v(-719.84, -465.81) * mm});
            skLineSegment(sketch, "E102.0.2.3", {"start": v(-750, -440) * mm, "end": v(-766.31, -440) * mm});
            skLineSegment(sketch, "E102.0.2.4", {"start": v(-750, -460) * mm, "end": v(-766.31, -460) * mm});
            skLineSegment(sketch, "E102.0.2.5", {"start": v(-733.54, -434.18) * mm, "end": v(-719.84, -434.18) * mm});
            skLineSegment(sketch, "E102.0.2.6", {"start": v(-766.31, -460) * mm, "end": v(-766.31, -450) * mm});
            skLineSegment(sketch, "E102.0.2.7", {"start": v(-750, -460) * mm, "end": v(-733.54, -460) * mm});
            skLineSegment(sketch, "E102.0.2.8", {"start": v(-719.84, -465.82) * mm, "end": v(-719.84, -450) * mm});
            skLineSegment(sketch, "E102.0.2.9", {"start": v(-750, -440) * mm, "end": v(-733.54, -440) * mm});
            skLineSegment(sketch, "E102.0.2.10", {"start": v(-733.54, -440) * mm, "end": v(-733.54, -434.18) * mm});
            skLineSegment(sketch, "E102.0.2.11", {"start": v(-733.54, -460) * mm, "end": v(-733.54, -465.81) * mm});
            skLineSegment(sketch, "E102.direction1", {"start": v(-766.31, -160) * mm, "end": v(-741.31, -160) * mm, "construction": true});
            skLineSegment(sketch, "E102.direction2", {"start": v(-766.31, -160) * mm, "end": v(-766.31, -310) * mm, "construction": true});
            skLineSegment(sketch, "E103.MirrorCS", {"start": v(733.54, -290) * mm, "end": v(733.54, -284.18) * mm});
            skLineSegment(sketch, "E104.MirrorCS", {"start": v(750, -160) * mm, "end": v(766.31, -160) * mm});
            skLineSegment(sketch, "E105.MirrorCS", {"start": v(766.31, -160) * mm, "end": v(741.31, -160) * mm, "construction": true});
            skLineSegment(sketch, "E106.MirrorCS", {"start": v(750, -310) * mm, "end": v(733.54, -310) * mm});
            skLineSegment(sketch, "E107.MirrorCS", {"start": v(733.54, -460) * mm, "end": v(733.54, -465.81) * mm});
            skLineSegment(sketch, "E108.MirrorCS", {"start": v(766.31, -160) * mm, "end": v(766.31, -150) * mm});
            skLineSegment(sketch, "E109.MirrorCS", {"start": v(750, -460) * mm, "end": v(766.31, -460) * mm});
            skLineSegment(sketch, "E110.MirrorCS", {"start": v(750, -310) * mm, "end": v(766.31, -310) * mm});
            skLineSegment(sketch, "E111.MirrorCS", {"start": v(750, -290) * mm, "end": v(766.31, -290) * mm});
            skLineSegment(sketch, "E112.MirrorCS", {"start": v(750, -440) * mm, "end": v(733.54, -440) * mm});
            skLineSegment(sketch, "E113.MirrorCS", {"start": v(733.54, -160) * mm, "end": v(733.54, -165.81) * mm});
            skLineSegment(sketch, "E114.MirrorCS", {"start": v(733.54, -284.18) * mm, "end": v(719.84, -284.18) * mm});
            skLineSegment(sketch, "E115.MirrorCS", {"start": v(750, -440) * mm, "end": v(766.31, -440) * mm});
            skLineSegment(sketch, "E116.MirrorCS", {"start": v(750, -290) * mm, "end": v(733.54, -290) * mm});
            skLineSegment(sketch, "E117.MirrorCS", {"start": v(733.54, -140) * mm, "end": v(733.54, -134.18) * mm});
            skLineSegment(sketch, "E118.MirrorCS", {"start": v(750, -450) * mm, "end": v(725, -450) * mm, "construction": true});
            skLineSegment(sketch, "E119.MirrorCS", {"start": v(750, -140) * mm, "end": v(733.54, -140) * mm});
            skLineSegment(sketch, "E120.MirrorCS", {"start": v(719.84, -315.81) * mm, "end": v(719.84, -300) * mm});
            skLineSegment(sketch, "E121.MirrorCS", {"start": v(719.84, -165.81) * mm, "end": v(719.84, -150) * mm});
            skLineSegment(sketch, "E122.MirrorCS", {"start": v(733.54, -465.81) * mm, "end": v(719.84, -465.81) * mm});
            skLineSegment(sketch, "E123.MirrorCS", {"start": v(750, -160) * mm, "end": v(733.54, -160) * mm});
            skLineSegment(sketch, "E124.MirrorCS", {"start": v(733.54, -310) * mm, "end": v(733.54, -315.81) * mm});
            skLineSegment(sketch, "E125.MirrorCS", {"start": v(719.84, -284.18) * mm, "end": v(719.84, -300) * mm});
            skLineSegment(sketch, "E126.MirrorCS", {"start": v(719.84, -465.81) * mm, "end": v(719.84, -450) * mm});
            skLineSegment(sketch, "E127.MirrorCS", {"start": v(750, -460) * mm, "end": v(733.54, -460) * mm});
            skLineSegment(sketch, "E128.MirrorCS", {"start": v(719.84, -434.18) * mm, "end": v(719.84, -450) * mm});
            skLineSegment(sketch, "E129.MirrorCS", {"start": v(733.54, -440) * mm, "end": v(733.54, -434.18) * mm});
            skLineSegment(sketch, "E130.MirrorCS", {"start": v(766.31, -310) * mm, "end": v(766.31, -300) * mm});
            skLineSegment(sketch, "E131.MirrorCS", {"start": v(750, -140) * mm, "end": v(766.31, -140) * mm});
            skLineSegment(sketch, "E132.MirrorCS", {"start": v(733.54, -165.81) * mm, "end": v(719.84, -165.81) * mm});
            skLineSegment(sketch, "E133.MirrorCS", {"start": v(733.54, -134.18) * mm, "end": v(719.84, -134.18) * mm});
            skLineSegment(sketch, "E134.MirrorCS", {"start": v(733.54, -315.81) * mm, "end": v(719.84, -315.81) * mm});
            skLineSegment(sketch, "E135.MirrorCS", {"start": v(719.84, -134.18) * mm, "end": v(719.84, -150) * mm});
            skLineSegment(sketch, "E136.MirrorCS", {"start": v(766.31, -140) * mm, "end": v(766.31, -150) * mm});
            skLineSegment(sketch, "E137.MirrorCS", {"start": v(766.31, -290) * mm, "end": v(766.31, -300) * mm});
            skLineSegment(sketch, "E138.MirrorCS", {"start": v(733.54, -434.18) * mm, "end": v(719.84, -434.18) * mm});
            skLineSegment(sketch, "E139.MirrorCS", {"start": v(766.31, -460) * mm, "end": v(766.31, -450) * mm});
            skLineSegment(sketch, "E140.MirrorCS", {"start": v(766.31, -440) * mm, "end": v(766.31, -450) * mm});
            skLineSegment(sketch, "E141.MirrorCS", {"start": v(766.31, -160) * mm, "end": v(766.31, -310) * mm, "construction": true});
            skLineSegment(sketch, "E142.MirrorCS", {"start": v(750, -450) * mm, "end": v(750, -300) * mm, "construction": true});
            skSolve(sketch);
        }
        {
            var Q0;
            Q0 = qSketchRegion(id + "F4", true);
            extrude(context, id + "F5", {"entities" : qUnion([Q0]), "operationType" : NewBodyOperationType.REMOVE, "endBound" : BoundingType.THROUGH_ALL, "oppositeDirection" : true, "depth" : 25 * mm});
        }
        {
            var Q0;
            Q0=makeQuery(id+"F5.boolean.opBoolean","MERGE",FACE,{"derivedFrom":[makeQuery(id+"F3.boolean.opBoolean","COPY",FACE,{"derivedFrom":makeQuery(id+"F3.opExtrude","SWEPT_FACE",FACE,{"disambiguationData":[OSD([sQuery(id+"F2.wireOp",EDGE,"E12"),sQuery(id+"F2.wireOp",EDGE,"E19.MirrorCS")])]})}),makeQuery(id+"F3.boolean.opBoolean","COPY",FACE,{"derivedFrom":makeQuery(id+"F3.opExtrude","SWEPT_FACE",FACE,{"disambiguationData":[OSD([sQuery(id+"F2.wireOp",EDGE,"E21.1.0.1"),sQuery(id+"F2.wireOp",EDGE,"E21.1.0.5")])]})}),makeQuery(id+"F3.boolean.opBoolean","COPY",FACE,{"derivedFrom":makeQuery(id+"F3.opExtrude","SWEPT_FACE",FACE,{"disambiguationData":[OSD([sQuery(id+"F2.wireOp",EDGE,"E21.2.0.1"),sQuery(id+"F2.wireOp",EDGE,"E21.2.0.5")])]})}),makeQuery(id+"F3.boolean.opBoolean","COPY",FACE,{"derivedFrom":makeQuery(id+"F3.opExtrude","SWEPT_FACE",FACE,{"disambiguationData":[OSD([sQuery(id+"F2.wireOp",EDGE,"E21.3.0.1"),sQuery(id+"F2.wireOp",EDGE,"E21.3.0.5")])]})}),makeQuery(id+"F5.opExtrude","SWEPT_FACE",FACE,{"disambiguationData":[OSD([sQuery(id+"F4.wireOp",EDGE,"E79"),sQuery(id+"F4.wireOp",EDGE,"E85.MirrorCS")])]}),makeQuery(id+"F5.opExtrude","SWEPT_FACE",FACE,{"disambiguationData":[OSD([sQuery(id+"F4.wireOp",EDGE,"E88.1.0.0"),sQuery(id+"F4.wireOp",EDGE,"E88.1.0.2")])]}),makeQuery(id+"F5.opExtrude","SWEPT_FACE",FACE,{"disambiguationData":[OSD([sQuery(id+"F4.wireOp",EDGE,"E88.2.0.0"),sQuery(id+"F4.wireOp",EDGE,"E88.2.0.2")])]}),makeQuery(id+"F5.opExtrude","SWEPT_FACE",FACE,{"disambiguationData":[OSD([sQuery(id+"F4.wireOp",EDGE,"E88.3.0.0"),sQuery(id+"F4.wireOp",EDGE,"E88.3.0.2")])]}),makeQuery(id+"F5.opExtrude","SWEPT_FACE",FACE,{"disambiguationData":[OSD([sQuery(id+"F4.wireOp",EDGE,"E88.4.0.0"),sQuery(id+"F4.wireOp",EDGE,"E88.4.0.2")])]}),makeQuery(id+"F5.opExtrude","SWEPT_FACE",FACE,{"disambiguationData":[OSD([sQuery(id+"F4.wireOp",EDGE,"E88.5.0.0"),sQuery(id+"F4.wireOp",EDGE,"E88.5.0.2")])]}),makeQuery(id+"F5.opExtrude","SWEPT_FACE",FACE,{"disambiguationData":[OSD([sQuery(id+"F4.wireOp",EDGE,"E88.6.0.0"),sQuery(id+"F4.wireOp",EDGE,"E88.6.0.2")])]}),makeQuery(id+"F5.opExtrude","SWEPT_FACE",FACE,{"disambiguationData":[OSD([sQuery(id+"F4.wireOp",EDGE,"E88.7.0.0"),sQuery(id+"F4.wireOp",EDGE,"E88.7.0.2")])]}),makeQuery(id+"F5.opExtrude","SWEPT_FACE",FACE,{"disambiguationData":[OSD([sQuery(id+"F4.wireOp",EDGE,"E88.8.0.0"),sQuery(id+"F4.wireOp",EDGE,"E88.8.0.2")])]})]});
            var sketch = newSketch(context, id + "F6", { "sketchPlane" : qUnion([Q0])});
            skLineSegment(sketch, "E143", {"start": v(-225, 750) * mm, "end": v(-225, -750) * mm, "construction": true});
            skLineSegment(sketch, "E144.1.0.0", {"start": v(-75, 750) * mm, "end": v(-75, -750) * mm, "construction": true});
            skLineSegment(sketch, "E144.2.0.0", {"start": v(75, 750) * mm, "end": v(75, -750) * mm, "construction": true});
            skLineSegment(sketch, "E144.3.0.0", {"start": v(225, 750) * mm, "end": v(225, -750) * mm, "construction": true});
            skLineSegment(sketch, "E144.direction1", {"start": v(-225, -750) * mm, "end": v(-75, -750) * mm, "construction": true});
            skLineSegment(sketch, "E145", {"start": v(-375, 600) * mm, "end": v(375, 600) * mm, "construction": true});
            skLineSegment(sketch, "E146", {"start": v(-235, 750) * mm, "end": v(-235, 733.54) * mm});
            skLineSegment(sketch, "E147", {"start": v(-235, 733.54) * mm, "end": v(-240.82, 733.54) * mm});
            skLineSegment(sketch, "E148", {"start": v(-240.82, 733.54) * mm, "end": v(-240.82, 719.84) * mm});
            skLineSegment(sketch, "E149", {"start": v(-240.82, 719.84) * mm, "end": v(-225, 719.84) * mm});
            skLineSegment(sketch, "E150", {"start": v(-235, 750) * mm, "end": v(-235, 760) * mm});
            skLineSegment(sketch, "E151", {"start": v(-235, 760) * mm, "end": v(-225, 760) * mm});
            skLineSegment(sketch, "E152.MirrorCS", {"start": v(-215, 750) * mm, "end": v(-215, 733.54) * mm});
            skLineSegment(sketch, "E153.MirrorCS", {"start": v(-215, 760) * mm, "end": v(-225, 760) * mm});
            skLineSegment(sketch, "E154.MirrorCS", {"start": v(-215, 750) * mm, "end": v(-215, 760) * mm});
            skLineSegment(sketch, "E155.MirrorCS", {"start": v(-209.18, 719.84) * mm, "end": v(-225, 719.84) * mm});
            skLineSegment(sketch, "E156.MirrorCS", {"start": v(-209.18, 733.54) * mm, "end": v(-209.18, 719.84) * mm});
            skLineSegment(sketch, "E157.MirrorCS", {"start": v(-215, 733.54) * mm, "end": v(-209.18, 733.54) * mm});
            skLineSegment(sketch, "E158.1.0.0", {"start": v(-85, 750) * mm, "end": v(-85, 760) * mm});
            skLineSegment(sketch, "E158.1.0.1", {"start": v(-65, 733.54) * mm, "end": v(-59.18, 733.54) * mm});
            skLineSegment(sketch, "E158.1.0.2", {"start": v(-90.82, 719.84) * mm, "end": v(-75, 719.84) * mm});
            skLineSegment(sketch, "E158.1.0.3", {"start": v(-59.18, 733.54) * mm, "end": v(-59.18, 719.84) * mm});
            skLineSegment(sketch, "E158.1.0.4", {"start": v(-85, 760) * mm, "end": v(-75, 760) * mm});
            skLineSegment(sketch, "E158.1.0.5", {"start": v(-90.82, 733.54) * mm, "end": v(-90.82, 719.84) * mm});
            skLineSegment(sketch, "E158.1.0.6", {"start": v(-59.18, 719.84) * mm, "end": v(-75, 719.84) * mm});
            skLineSegment(sketch, "E158.1.0.7", {"start": v(-65, 750) * mm, "end": v(-65, 760) * mm});
            skLineSegment(sketch, "E158.1.0.8", {"start": v(-85, 733.54) * mm, "end": v(-90.82, 733.54) * mm});
            skLineSegment(sketch, "E158.1.0.9", {"start": v(-65, 760) * mm, "end": v(-75, 760) * mm});
            skLineSegment(sketch, "E158.1.0.10", {"start": v(-85, 750) * mm, "end": v(-85, 733.54) * mm});
            skLineSegment(sketch, "E158.1.0.11", {"start": v(-65, 750) * mm, "end": v(-65, 733.54) * mm});
            skLineSegment(sketch, "E158.2.0.0", {"start": v(65, 750) * mm, "end": v(65, 760) * mm});
            skLineSegment(sketch, "E158.2.0.1", {"start": v(85, 733.54) * mm, "end": v(90.82, 733.54) * mm});
            skLineSegment(sketch, "E158.2.0.2", {"start": v(59.18, 719.84) * mm, "end": v(75, 719.84) * mm});
            skLineSegment(sketch, "E158.2.0.3", {"start": v(90.82, 733.54) * mm, "end": v(90.82, 719.84) * mm});
            skLineSegment(sketch, "E158.2.0.4", {"start": v(65, 760) * mm, "end": v(75, 760) * mm});
            skLineSegment(sketch, "E158.2.0.5", {"start": v(59.18, 733.54) * mm, "end": v(59.18, 719.84) * mm});
            skLineSegment(sketch, "E158.2.0.6", {"start": v(90.82, 719.84) * mm, "end": v(75, 719.84) * mm});
            skLineSegment(sketch, "E158.2.0.7", {"start": v(85, 750) * mm, "end": v(85, 760) * mm});
            skLineSegment(sketch, "E158.2.0.8", {"start": v(65, 733.54) * mm, "end": v(59.18, 733.54) * mm});
            skLineSegment(sketch, "E158.2.0.9", {"start": v(85, 760) * mm, "end": v(75, 760) * mm});
            skLineSegment(sketch, "E158.2.0.10", {"start": v(65, 750) * mm, "end": v(65, 733.54) * mm});
            skLineSegment(sketch, "E158.2.0.11", {"start": v(85, 750) * mm, "end": v(85, 733.54) * mm});
            skLineSegment(sketch, "E158.3.0.0", {"start": v(215, 750) * mm, "end": v(215, 760) * mm});
            skLineSegment(sketch, "E158.3.0.1", {"start": v(235, 733.54) * mm, "end": v(240.82, 733.54) * mm});
            skLineSegment(sketch, "E158.3.0.2", {"start": v(209.18, 719.84) * mm, "end": v(225, 719.84) * mm});
            skLineSegment(sketch, "E158.3.0.3", {"start": v(240.82, 733.54) * mm, "end": v(240.82, 719.84) * mm});
            skLineSegment(sketch, "E158.3.0.4", {"start": v(215, 760) * mm, "end": v(225, 760) * mm});
            skLineSegment(sketch, "E158.3.0.5", {"start": v(209.18, 733.54) * mm, "end": v(209.18, 719.84) * mm});
            skLineSegment(sketch, "E158.3.0.6", {"start": v(240.82, 719.84) * mm, "end": v(225, 719.84) * mm});
            skLineSegment(sketch, "E158.3.0.7", {"start": v(235, 750) * mm, "end": v(235, 760) * mm});
            skLineSegment(sketch, "E158.3.0.8", {"start": v(215, 733.54) * mm, "end": v(209.18, 733.54) * mm});
            skLineSegment(sketch, "E158.3.0.9", {"start": v(235, 760) * mm, "end": v(225, 760) * mm});
            skLineSegment(sketch, "E158.3.0.10", {"start": v(215, 750) * mm, "end": v(215, 733.54) * mm});
            skLineSegment(sketch, "E158.3.0.11", {"start": v(235, 750) * mm, "end": v(235, 733.54) * mm});
            skLineSegment(sketch, "E158.direction1", {"start": v(-240.82, 719.84) * mm, "end": v(-90.82, 719.84) * mm, "construction": true});
            skLineSegment(sketch, "E159", {"start": v(-375, 590) * mm, "end": v(-358.54, 590) * mm});
            skLineSegment(sketch, "E160", {"start": v(-358.54, 590) * mm, "end": v(-358.54, 584.18) * mm});
            skLineSegment(sketch, "E161", {"start": v(-358.54, 584.18) * mm, "end": v(-344.84, 584.18) * mm});
            skLineSegment(sketch, "E162", {"start": v(-344.84, 584.18) * mm, "end": v(-344.84, 600) * mm});
            skLineSegment(sketch, "E163", {"start": v(-375, 590) * mm, "end": v(-385, 590) * mm});
            skLineSegment(sketch, "E164", {"start": v(-385, 590) * mm, "end": v(-385, 600) * mm});
            skLineSegment(sketch, "E165.MirrorCS", {"start": v(-375, 610) * mm, "end": v(-358.54, 610) * mm});
            skLineSegment(sketch, "E166.MirrorCS", {"start": v(-358.54, 610) * mm, "end": v(-358.54, 615.82) * mm});
            skLineSegment(sketch, "E167.MirrorCS", {"start": v(-358.54, 615.82) * mm, "end": v(-344.84, 615.82) * mm});
            skLineSegment(sketch, "E168.MirrorCS", {"start": v(-344.84, 615.82) * mm, "end": v(-344.84, 600) * mm});
            skLineSegment(sketch, "E169.MirrorCS", {"start": v(-375, 610) * mm, "end": v(-385, 610) * mm});
            skLineSegment(sketch, "E170.MirrorCS", {"start": v(-385, 610) * mm, "end": v(-385, 600) * mm});
            skLineSegment(sketch, "E171.0.1.0", {"start": v(-375, 440) * mm, "end": v(-358.54, 440) * mm});
            skLineSegment(sketch, "E171.0.1.1", {"start": v(-358.54, 434.18) * mm, "end": v(-344.84, 434.18) * mm});
            skLineSegment(sketch, "E171.0.1.2", {"start": v(-358.54, 440) * mm, "end": v(-358.54, 434.18) * mm});
            skLineSegment(sketch, "E171.0.1.3", {"start": v(-344.84, 434.18) * mm, "end": v(-344.84, 450) * mm});
            skLineSegment(sketch, "E171.0.1.4", {"start": v(-375, 440) * mm, "end": v(-385, 440) * mm});
            skLineSegment(sketch, "E171.0.1.5", {"start": v(-385, 440) * mm, "end": v(-385, 450) * mm});
            skLineSegment(sketch, "E171.0.1.6", {"start": v(-375, 460) * mm, "end": v(-358.54, 460) * mm});
            skLineSegment(sketch, "E171.0.1.7", {"start": v(-358.54, 460) * mm, "end": v(-358.54, 465.81) * mm});
            skLineSegment(sketch, "E171.0.1.8", {"start": v(-358.54, 465.81) * mm, "end": v(-344.84, 465.81) * mm});
            skLineSegment(sketch, "E171.0.1.9", {"start": v(-344.84, 465.81) * mm, "end": v(-344.84, 450) * mm});
            skLineSegment(sketch, "E171.0.1.10", {"start": v(-385, 460) * mm, "end": v(-385, 450) * mm});
            skLineSegment(sketch, "E171.0.1.11", {"start": v(-375, 460) * mm, "end": v(-385, 460) * mm});
            skLineSegment(sketch, "E171.0.2.0", {"start": v(-375, 290) * mm, "end": v(-358.54, 290) * mm});
            skLineSegment(sketch, "E171.0.2.1", {"start": v(-358.54, 284.18) * mm, "end": v(-344.84, 284.18) * mm});
            skLineSegment(sketch, "E171.0.2.2", {"start": v(-358.54, 290) * mm, "end": v(-358.54, 284.18) * mm});
            skLineSegment(sketch, "E171.0.2.3", {"start": v(-344.84, 284.18) * mm, "end": v(-344.84, 300) * mm});
            skLineSegment(sketch, "E171.0.2.4", {"start": v(-375, 290) * mm, "end": v(-385, 290) * mm});
            skLineSegment(sketch, "E171.0.2.5", {"start": v(-385, 290) * mm, "end": v(-385, 300) * mm});
            skLineSegment(sketch, "E171.0.2.6", {"start": v(-375, 310) * mm, "end": v(-358.54, 310) * mm});
            skLineSegment(sketch, "E171.0.2.7", {"start": v(-358.54, 310) * mm, "end": v(-358.54, 315.81) * mm});
            skLineSegment(sketch, "E171.0.2.8", {"start": v(-358.54, 315.81) * mm, "end": v(-344.84, 315.81) * mm});
            skLineSegment(sketch, "E171.0.2.9", {"start": v(-344.84, 315.81) * mm, "end": v(-344.84, 300) * mm});
            skLineSegment(sketch, "E171.0.2.10", {"start": v(-385, 310) * mm, "end": v(-385, 300) * mm});
            skLineSegment(sketch, "E171.0.2.11", {"start": v(-375, 310) * mm, "end": v(-385, 310) * mm});
            skLineSegment(sketch, "E171.0.3.0", {"start": v(-375, 140) * mm, "end": v(-358.54, 140) * mm});
            skLineSegment(sketch, "E171.0.3.1", {"start": v(-358.54, 134.18) * mm, "end": v(-344.84, 134.18) * mm});
            skLineSegment(sketch, "E171.0.3.2", {"start": v(-358.54, 140) * mm, "end": v(-358.54, 134.18) * mm});
            skLineSegment(sketch, "E171.0.3.3", {"start": v(-344.84, 134.18) * mm, "end": v(-344.84, 150) * mm});
            skLineSegment(sketch, "E171.0.3.4", {"start": v(-375, 140) * mm, "end": v(-385, 140) * mm});
            skLineSegment(sketch, "E171.0.3.5", {"start": v(-385, 140) * mm, "end": v(-385, 150) * mm});
            skLineSegment(sketch, "E171.0.3.6", {"start": v(-375, 160) * mm, "end": v(-358.54, 160) * mm});
            skLineSegment(sketch, "E171.0.3.7", {"start": v(-358.54, 160) * mm, "end": v(-358.54, 165.81) * mm});
            skLineSegment(sketch, "E171.0.3.8", {"start": v(-358.54, 165.81) * mm, "end": v(-344.84, 165.81) * mm});
            skLineSegment(sketch, "E171.0.3.9", {"start": v(-344.84, 165.81) * mm, "end": v(-344.84, 150) * mm});
            skLineSegment(sketch, "E171.0.3.10", {"start": v(-385, 160) * mm, "end": v(-385, 150) * mm});
            skLineSegment(sketch, "E171.0.3.11", {"start": v(-375, 160) * mm, "end": v(-385, 160) * mm});
            skLineSegment(sketch, "E171.0.4.0", {"start": v(-375, -10) * mm, "end": v(-358.54, -10) * mm});
            skLineSegment(sketch, "E171.0.4.1", {"start": v(-358.54, -15.82) * mm, "end": v(-344.84, -15.82) * mm});
            skLineSegment(sketch, "E171.0.4.2", {"start": v(-358.54, -10) * mm, "end": v(-358.54, -15.82) * mm});
            skLineSegment(sketch, "E171.0.4.3", {"start": v(-344.84, -15.82) * mm, "end": v(-344.84, 0) * mm});
            skLineSegment(sketch, "E171.0.4.4", {"start": v(-375, -10) * mm, "end": v(-385, -10) * mm});
            skLineSegment(sketch, "E171.0.4.5", {"start": v(-385, -10) * mm, "end": v(-385, 0) * mm});
            skLineSegment(sketch, "E171.0.4.6", {"start": v(-375, 10) * mm, "end": v(-358.54, 10) * mm});
            skLineSegment(sketch, "E171.0.4.7", {"start": v(-358.54, 10) * mm, "end": v(-358.54, 15.81) * mm});
            skLineSegment(sketch, "E171.0.4.8", {"start": v(-358.54, 15.81) * mm, "end": v(-344.84, 15.81) * mm});
            skLineSegment(sketch, "E171.0.4.9", {"start": v(-344.84, 15.81) * mm, "end": v(-344.84, 0) * mm});
            skLineSegment(sketch, "E171.0.4.10", {"start": v(-385, 10) * mm, "end": v(-385, 0) * mm});
            skLineSegment(sketch, "E171.0.4.11", {"start": v(-375, 10) * mm, "end": v(-385, 10) * mm});
            skLineSegment(sketch, "E171.0.5.0", {"start": v(-375, -160) * mm, "end": v(-358.54, -160) * mm});
            skLineSegment(sketch, "E171.0.5.1", {"start": v(-358.54, -165.82) * mm, "end": v(-344.84, -165.82) * mm});
            skLineSegment(sketch, "E171.0.5.2", {"start": v(-358.54, -160) * mm, "end": v(-358.54, -165.82) * mm});
            skLineSegment(sketch, "E171.0.5.3", {"start": v(-344.84, -165.82) * mm, "end": v(-344.84, -150) * mm});
            skLineSegment(sketch, "E171.0.5.4", {"start": v(-375, -160) * mm, "end": v(-385, -160) * mm});
            skLineSegment(sketch, "E171.0.5.5", {"start": v(-385, -160) * mm, "end": v(-385, -150) * mm});
            skLineSegment(sketch, "E171.0.5.6", {"start": v(-375, -140) * mm, "end": v(-358.54, -140) * mm});
            skLineSegment(sketch, "E171.0.5.7", {"start": v(-358.54, -140) * mm, "end": v(-358.54, -134.19) * mm});
            skLineSegment(sketch, "E171.0.5.8", {"start": v(-358.54, -134.19) * mm, "end": v(-344.84, -134.19) * mm});
            skLineSegment(sketch, "E171.0.5.9", {"start": v(-344.84, -134.19) * mm, "end": v(-344.84, -150) * mm});
            skLineSegment(sketch, "E171.0.5.10", {"start": v(-385, -140) * mm, "end": v(-385, -150) * mm});
            skLineSegment(sketch, "E171.0.5.11", {"start": v(-375, -140) * mm, "end": v(-385, -140) * mm});
            skLineSegment(sketch, "E171.0.6.0", {"start": v(-375, -310) * mm, "end": v(-358.54, -310) * mm});
            skLineSegment(sketch, "E171.0.6.1", {"start": v(-358.54, -315.82) * mm, "end": v(-344.84, -315.82) * mm});
            skLineSegment(sketch, "E171.0.6.2", {"start": v(-358.54, -310) * mm, "end": v(-358.54, -315.82) * mm});
            skLineSegment(sketch, "E171.0.6.3", {"start": v(-344.84, -315.82) * mm, "end": v(-344.84, -300) * mm});
            skLineSegment(sketch, "E171.0.6.4", {"start": v(-375, -310) * mm, "end": v(-385, -310) * mm});
            skLineSegment(sketch, "E171.0.6.5", {"start": v(-385, -310) * mm, "end": v(-385, -300) * mm});
            skLineSegment(sketch, "E171.0.6.6", {"start": v(-375, -290) * mm, "end": v(-358.54, -290) * mm});
            skLineSegment(sketch, "E171.0.6.7", {"start": v(-358.54, -290) * mm, "end": v(-358.54, -284.19) * mm});
            skLineSegment(sketch, "E171.0.6.8", {"start": v(-358.54, -284.19) * mm, "end": v(-344.84, -284.19) * mm});
            skLineSegment(sketch, "E171.0.6.9", {"start": v(-344.84, -284.19) * mm, "end": v(-344.84, -300) * mm});
            skLineSegment(sketch, "E171.0.6.10", {"start": v(-385, -290) * mm, "end": v(-385, -300) * mm});
            skLineSegment(sketch, "E171.0.6.11", {"start": v(-375, -290) * mm, "end": v(-385, -290) * mm});
            skLineSegment(sketch, "E171.0.7.0", {"start": v(-375, -460) * mm, "end": v(-358.54, -460) * mm});
            skLineSegment(sketch, "E171.0.7.1", {"start": v(-358.54, -465.82) * mm, "end": v(-344.84, -465.82) * mm});
            skLineSegment(sketch, "E171.0.7.2", {"start": v(-358.54, -460) * mm, "end": v(-358.54, -465.82) * mm});
            skLineSegment(sketch, "E171.0.7.3", {"start": v(-344.84, -465.82) * mm, "end": v(-344.84, -450) * mm});
            skLineSegment(sketch, "E171.0.7.4", {"start": v(-375, -460) * mm, "end": v(-385, -460) * mm});
            skLineSegment(sketch, "E171.0.7.5", {"start": v(-385, -460) * mm, "end": v(-385, -450) * mm});
            skLineSegment(sketch, "E171.0.7.6", {"start": v(-375, -440) * mm, "end": v(-358.54, -440) * mm});
            skLineSegment(sketch, "E171.0.7.7", {"start": v(-358.54, -440) * mm, "end": v(-358.54, -434.19) * mm});
            skLineSegment(sketch, "E171.0.7.8", {"start": v(-358.54, -434.19) * mm, "end": v(-344.84, -434.19) * mm});
            skLineSegment(sketch, "E171.0.7.9", {"start": v(-344.84, -434.19) * mm, "end": v(-344.84, -450) * mm});
            skLineSegment(sketch, "E171.0.7.10", {"start": v(-385, -440) * mm, "end": v(-385, -450) * mm});
            skLineSegment(sketch, "E171.0.7.11", {"start": v(-375, -440) * mm, "end": v(-385, -440) * mm});
            skLineSegment(sketch, "E171.0.8.0", {"start": v(-375, -610) * mm, "end": v(-358.54, -610) * mm});
            skLineSegment(sketch, "E171.0.8.1", {"start": v(-358.54, -615.82) * mm, "end": v(-344.84, -615.82) * mm});
            skLineSegment(sketch, "E171.0.8.2", {"start": v(-358.54, -610) * mm, "end": v(-358.54, -615.82) * mm});
            skLineSegment(sketch, "E171.0.8.3", {"start": v(-344.84, -615.82) * mm, "end": v(-344.84, -600) * mm});
            skLineSegment(sketch, "E171.0.8.4", {"start": v(-375, -610) * mm, "end": v(-385, -610) * mm});
            skLineSegment(sketch, "E171.0.8.5", {"start": v(-385, -610) * mm, "end": v(-385, -600) * mm});
            skLineSegment(sketch, "E171.0.8.6", {"start": v(-375, -590) * mm, "end": v(-358.54, -590) * mm});
            skLineSegment(sketch, "E171.0.8.7", {"start": v(-358.54, -590) * mm, "end": v(-358.54, -584.19) * mm});
            skLineSegment(sketch, "E171.0.8.8", {"start": v(-358.54, -584.19) * mm, "end": v(-344.84, -584.19) * mm});
            skLineSegment(sketch, "E171.0.8.9", {"start": v(-344.84, -584.19) * mm, "end": v(-344.84, -600) * mm});
            skLineSegment(sketch, "E171.0.8.10", {"start": v(-385, -590) * mm, "end": v(-385, -600) * mm});
            skLineSegment(sketch, "E171.0.8.11", {"start": v(-375, -590) * mm, "end": v(-385, -590) * mm});
            skLineSegment(sketch, "E171.direction2", {"start": v(-385, 590) * mm, "end": v(-385, 440) * mm, "construction": true});
            skPoint(sketch, "E172.startSnap0", {"position": v(0, 315.81) * mm});
            skLineSegment(sketch, "E173.MirrorCS", {"start": v(375, -290) * mm, "end": v(385, -290) * mm});
            skLineSegment(sketch, "E174.MirrorCS", {"start": v(344.84, -284.19) * mm, "end": v(344.84, -300) * mm});
            skLineSegment(sketch, "E175.MirrorCS", {"start": v(358.54, -284.19) * mm, "end": v(344.84, -284.19) * mm});
            skLineSegment(sketch, "E176.MirrorCS", {"start": v(375, 610) * mm, "end": v(385, 610) * mm});
            skLineSegment(sketch, "E177.MirrorCS", {"start": v(358.54, -290) * mm, "end": v(358.54, -284.19) * mm});
            skLineSegment(sketch, "E178.MirrorCS", {"start": v(358.54, 134.18) * mm, "end": v(344.84, 134.18) * mm});
            skLineSegment(sketch, "E179.MirrorCS", {"start": v(344.84, 615.82) * mm, "end": v(344.84, 600) * mm});
            skLineSegment(sketch, "E180.MirrorCS", {"start": v(375, -290) * mm, "end": v(358.54, -290) * mm});
            skLineSegment(sketch, "E181.MirrorCS", {"start": v(358.54, 615.81) * mm, "end": v(344.84, 615.81) * mm});
            skLineSegment(sketch, "E182.MirrorCS", {"start": v(358.54, -15.82) * mm, "end": v(344.84, -15.82) * mm});
            skLineSegment(sketch, "E183.MirrorCS", {"start": v(358.54, 610) * mm, "end": v(358.54, 615.82) * mm});
            skLineSegment(sketch, "E184.MirrorCS", {"start": v(375, -310) * mm, "end": v(385, -310) * mm});
            skLineSegment(sketch, "E185.MirrorCS", {"start": v(375, 610) * mm, "end": v(358.54, 610) * mm});
            skLineSegment(sketch, "E186.MirrorCS", {"start": v(344.84, -315.82) * mm, "end": v(344.84, -300) * mm});
            skLineSegment(sketch, "E187.MirrorCS", {"start": v(358.54, -310) * mm, "end": v(358.54, -315.82) * mm});
            skLineSegment(sketch, "E188.MirrorCS", {"start": v(375, 590) * mm, "end": v(385, 590) * mm});
            skLineSegment(sketch, "E189.MirrorCS", {"start": v(358.54, -615.82) * mm, "end": v(344.84, -615.82) * mm});
            skLineSegment(sketch, "E190.MirrorCS", {"start": v(358.54, 590) * mm, "end": v(358.54, 584.18) * mm});
            skLineSegment(sketch, "E191.MirrorCS", {"start": v(375, -310) * mm, "end": v(358.54, -310) * mm});
            skLineSegment(sketch, "E192.MirrorCS", {"start": v(375, 590) * mm, "end": v(358.54, 590) * mm});
            skLineSegment(sketch, "E193.MirrorCS", {"start": v(344.84, 584.18) * mm, "end": v(344.84, 600) * mm});
            skLineSegment(sketch, "E194.MirrorCS", {"start": v(375, 140) * mm, "end": v(385, 140) * mm});
            skLineSegment(sketch, "E195.MirrorCS", {"start": v(375, 10) * mm, "end": v(358.54, 10) * mm});
            skLineSegment(sketch, "E196.MirrorCS", {"start": v(344.84, 134.18) * mm, "end": v(344.84, 150) * mm});
            skLineSegment(sketch, "E197.MirrorCS", {"start": v(385, 610) * mm, "end": v(385, 600) * mm});
            skLineSegment(sketch, "E198.MirrorCS", {"start": v(358.54, 284.18) * mm, "end": v(344.84, 284.18) * mm});
            skLineSegment(sketch, "E199.MirrorCS", {"start": v(358.54, 140) * mm, "end": v(358.54, 134.18) * mm});
            skLineSegment(sketch, "E200.MirrorCS", {"start": v(375, -10) * mm, "end": v(385, -10) * mm});
            skLineSegment(sketch, "E201.MirrorCS", {"start": v(375, -590) * mm, "end": v(385, -590) * mm});
            skLineSegment(sketch, "E202.MirrorCS", {"start": v(344.84, -15.82) * mm, "end": v(344.84, 0) * mm});
            skLineSegment(sketch, "E203.MirrorCS", {"start": v(375, 140) * mm, "end": v(358.54, 140) * mm});
            skLineSegment(sketch, "E204.MirrorCS", {"start": v(358.54, -10) * mm, "end": v(358.54, -15.82) * mm});
            skLineSegment(sketch, "E205.MirrorCS", {"start": v(344.84, -584.19) * mm, "end": v(344.84, -600) * mm});
            skLineSegment(sketch, "E206.MirrorCS", {"start": v(375, -10) * mm, "end": v(358.54, -10) * mm});
            skLineSegment(sketch, "E207.MirrorCS", {"start": v(358.54, -590) * mm, "end": v(358.54, -584.19) * mm});
            skLineSegment(sketch, "E208.MirrorCS", {"start": v(375, -590) * mm, "end": v(358.54, -590) * mm});
            skLineSegment(sketch, "E209.MirrorCS", {"start": v(385, 590) * mm, "end": v(385, 600) * mm});
            skLineSegment(sketch, "E210.MirrorCS", {"start": v(375, 160) * mm, "end": v(385, 160) * mm});
            skLineSegment(sketch, "E211.MirrorCS", {"start": v(358.54, 440) * mm, "end": v(358.54, 434.18) * mm});
            skLineSegment(sketch, "E212.MirrorCS", {"start": v(375, 160) * mm, "end": v(358.54, 160) * mm});
            skLineSegment(sketch, "E213.MirrorCS", {"start": v(375, -610) * mm, "end": v(358.54, -610) * mm});
            skLineSegment(sketch, "E214.MirrorCS", {"start": v(358.54, 160) * mm, "end": v(358.54, 165.81) * mm});
            skLineSegment(sketch, "E215.MirrorCS", {"start": v(375, 440) * mm, "end": v(385, 440) * mm});
            skLineSegment(sketch, "E216.MirrorCS", {"start": v(358.54, -610) * mm, "end": v(358.54, -615.82) * mm});
            skLineSegment(sketch, "E217.MirrorCS", {"start": v(375, 10) * mm, "end": v(385, 10) * mm});
            skLineSegment(sketch, "E218.MirrorCS", {"start": v(344.84, 165.81) * mm, "end": v(344.84, 150) * mm});
            skLineSegment(sketch, "E219.MirrorCS", {"start": v(344.84, -615.82) * mm, "end": v(344.84, -600) * mm});
            skLineSegment(sketch, "E220.MirrorCS", {"start": v(375, -610) * mm, "end": v(385, -610) * mm});
            skLineSegment(sketch, "E221.MirrorCS", {"start": v(385, 140) * mm, "end": v(385, 150) * mm});
            skLineSegment(sketch, "E222.MirrorCS", {"start": v(358.54, 10) * mm, "end": v(358.54, 15.81) * mm});
            skLineSegment(sketch, "E223.MirrorCS", {"start": v(344.84, -134.19) * mm, "end": v(344.84, -150) * mm});
            skLineSegment(sketch, "E224.MirrorCS", {"start": v(344.84, 284.18) * mm, "end": v(344.84, 300) * mm});
            skLineSegment(sketch, "E225.MirrorCS", {"start": v(358.54, -134.19) * mm, "end": v(344.84, -134.19) * mm});
            skLineSegment(sketch, "E226.MirrorCS", {"start": v(385, -290) * mm, "end": v(385, -300) * mm});
            skLineSegment(sketch, "E227.MirrorCS", {"start": v(375, 440) * mm, "end": v(358.54, 440) * mm});
            skLineSegment(sketch, "E228.MirrorCS", {"start": v(358.54, 290) * mm, "end": v(358.54, 284.18) * mm});
            skLineSegment(sketch, "E229.MirrorCS", {"start": v(385, -10) * mm, "end": v(385, 0) * mm});
            skLineSegment(sketch, "E230.MirrorCS", {"start": v(358.54, -140) * mm, "end": v(358.54, -134.19) * mm});
            skLineSegment(sketch, "E231.MirrorCS", {"start": v(375, -440) * mm, "end": v(385, -440) * mm});
            skLineSegment(sketch, "E232.MirrorCS", {"start": v(385, -440) * mm, "end": v(385, -450) * mm});
            skLineSegment(sketch, "E233.MirrorCS", {"start": v(375, 290) * mm, "end": v(358.54, 290) * mm});
            skLineSegment(sketch, "E234.MirrorCS", {"start": v(375, -140) * mm, "end": v(358.54, -140) * mm});
            skLineSegment(sketch, "E235.MirrorCS", {"start": v(344.84, -434.19) * mm, "end": v(344.84, -450) * mm});
            skLineSegment(sketch, "E236.MirrorCS", {"start": v(385, -160) * mm, "end": v(385, -150) * mm});
            skLineSegment(sketch, "E237.MirrorCS", {"start": v(358.54, -434.19) * mm, "end": v(344.84, -434.19) * mm});
            skLineSegment(sketch, "E238.MirrorCS", {"start": v(385, -590) * mm, "end": v(385, -600) * mm});
            skLineSegment(sketch, "E239.MirrorCS", {"start": v(375, -160) * mm, "end": v(385, -160) * mm});
            skLineSegment(sketch, "E240.MirrorCS", {"start": v(385, -310) * mm, "end": v(385, -300) * mm});
            skLineSegment(sketch, "E241.MirrorCS", {"start": v(358.54, -440) * mm, "end": v(358.54, -434.19) * mm});
            skLineSegment(sketch, "E242.MirrorCS", {"start": v(375, 460) * mm, "end": v(385, 460) * mm});
            skLineSegment(sketch, "E243.MirrorCS", {"start": v(344.84, -165.82) * mm, "end": v(344.84, -150) * mm});
            skLineSegment(sketch, "E244.MirrorCS", {"start": v(375, -440) * mm, "end": v(358.54, -440) * mm});
            skLineSegment(sketch, "E245.MirrorCS", {"start": v(385, 460) * mm, "end": v(385, 450) * mm});
            skLineSegment(sketch, "E246.MirrorCS", {"start": v(358.54, -160) * mm, "end": v(358.54, -165.82) * mm});
            skLineSegment(sketch, "E247.MirrorCS", {"start": v(385, -460) * mm, "end": v(385, -450) * mm});
            skLineSegment(sketch, "E248.MirrorCS", {"start": v(344.84, 465.81) * mm, "end": v(344.84, 450) * mm});
            skLineSegment(sketch, "E249.MirrorCS", {"start": v(375, 310) * mm, "end": v(385, 310) * mm});
            skLineSegment(sketch, "E250.MirrorCS", {"start": v(375, -160) * mm, "end": v(358.54, -160) * mm});
            skLineSegment(sketch, "E251.MirrorCS", {"start": v(375, -460) * mm, "end": v(385, -460) * mm});
            skLineSegment(sketch, "E252.MirrorCS", {"start": v(358.54, 465.81) * mm, "end": v(344.84, 465.81) * mm});
            skLineSegment(sketch, "E253.MirrorCS", {"start": v(385, 310) * mm, "end": v(385, 300) * mm});
            skLineSegment(sketch, "E254.MirrorCS", {"start": v(385, -610) * mm, "end": v(385, -600) * mm});
            skLineSegment(sketch, "E255.MirrorCS", {"start": v(358.54, -315.82) * mm, "end": v(344.84, -315.82) * mm});
            skLineSegment(sketch, "E256.MirrorCS", {"start": v(344.84, -465.82) * mm, "end": v(344.84, -450) * mm});
            skLineSegment(sketch, "E257.MirrorCS", {"start": v(358.54, 460) * mm, "end": v(358.54, 465.81) * mm});
            skLineSegment(sketch, "E258.MirrorCS", {"start": v(344.84, 315.81) * mm, "end": v(344.84, 300) * mm});
            skLineSegment(sketch, "E259.MirrorCS", {"start": v(375, 290) * mm, "end": v(385, 290) * mm});
            skLineSegment(sketch, "E260.MirrorCS", {"start": v(385, -140) * mm, "end": v(385, -150) * mm});
            skLineSegment(sketch, "E261.MirrorCS", {"start": v(375, -140) * mm, "end": v(385, -140) * mm});
            skLineSegment(sketch, "E262.MirrorCS", {"start": v(375, 310) * mm, "end": v(358.54, 310) * mm});
            skLineSegment(sketch, "E263.MirrorCS", {"start": v(375, -460) * mm, "end": v(358.54, -460) * mm});
            skLineSegment(sketch, "E264.MirrorCS", {"start": v(385, 10) * mm, "end": v(385, 0) * mm});
            skLineSegment(sketch, "E265.MirrorCS", {"start": v(358.54, 165.81) * mm, "end": v(344.84, 165.81) * mm});
            skLineSegment(sketch, "E266.MirrorCS", {"start": v(385, 160) * mm, "end": v(385, 150) * mm});
            skLineSegment(sketch, "E267.MirrorCS", {"start": v(344.84, 434.18) * mm, "end": v(344.84, 450) * mm});
            skLineSegment(sketch, "E268.MirrorCS", {"start": v(385, 290) * mm, "end": v(385, 300) * mm});
            skLineSegment(sketch, "E269.MirrorCS", {"start": v(358.54, 310) * mm, "end": v(358.54, 315.81) * mm});
            skLineSegment(sketch, "E270.MirrorCS", {"start": v(385, 440) * mm, "end": v(385, 450) * mm});
            skLineSegment(sketch, "E271.MirrorCS", {"start": v(358.54, 584.18) * mm, "end": v(344.84, 584.18) * mm});
            skLineSegment(sketch, "E272.MirrorCS", {"start": v(358.54, -460) * mm, "end": v(358.54, -465.82) * mm});
            skLineSegment(sketch, "E273.MirrorCS", {"start": v(358.54, 315.81) * mm, "end": v(344.84, 315.81) * mm});
            skLineSegment(sketch, "E274.MirrorCS", {"start": v(375, 460) * mm, "end": v(358.54, 460) * mm});
            skLineSegment(sketch, "E275.MirrorCS", {"start": v(358.54, 434.18) * mm, "end": v(344.84, 434.18) * mm});
            skLineSegment(sketch, "E276.MirrorCS", {"start": v(358.54, -165.82) * mm, "end": v(344.84, -165.82) * mm});
            skLineSegment(sketch, "E277.MirrorCS", {"start": v(358.54, 15.81) * mm, "end": v(344.84, 15.81) * mm});
            skLineSegment(sketch, "E278.MirrorCS", {"start": v(358.54, -465.82) * mm, "end": v(344.84, -465.82) * mm});
            skLineSegment(sketch, "E279.MirrorCS", {"start": v(358.54, -584.19) * mm, "end": v(344.84, -584.19) * mm});
            skLineSegment(sketch, "E280.MirrorCS", {"start": v(344.84, 15.81) * mm, "end": v(344.84, 0) * mm});
            skLineSegment(sketch, "E281.MirrorCS", {"start": v(385, 590) * mm, "end": v(385, 440) * mm, "construction": true});
            skLineSegment(sketch, "E282", {"start": v(-375, 0) * mm, "end": v(375, 0) * mm, "construction": true});
            skLineSegment(sketch, "E283.MirrorCS", {"start": v(-90.82, -733.54) * mm, "end": v(-90.82, -719.84) * mm});
            skLineSegment(sketch, "E284.MirrorCS", {"start": v(-235, -750) * mm, "end": v(-235, -733.54) * mm});
            skLineSegment(sketch, "E285.MirrorCS", {"start": v(-85, -733.54) * mm, "end": v(-90.82, -733.54) * mm});
            skLineSegment(sketch, "E286.MirrorCS", {"start": v(-85, -750) * mm, "end": v(-85, -733.54) * mm});
            skLineSegment(sketch, "E287.MirrorCS", {"start": v(-235, -750) * mm, "end": v(-235, -760) * mm});
            skLineSegment(sketch, "E288.MirrorCS", {"start": v(85, -733.54) * mm, "end": v(90.82, -733.54) * mm});
            skLineSegment(sketch, "E289.MirrorCS", {"start": v(-215, -750) * mm, "end": v(-215, -733.54) * mm});
            skLineSegment(sketch, "E290.MirrorCS", {"start": v(-235, -733.54) * mm, "end": v(-240.82, -733.54) * mm});
            skLineSegment(sketch, "E291.MirrorCS", {"start": v(-215, -750) * mm, "end": v(-215, -760) * mm});
            skLineSegment(sketch, "E292.MirrorCS", {"start": v(-240.82, -733.54) * mm, "end": v(-240.82, -719.84) * mm});
            skLineSegment(sketch, "E293.MirrorCS", {"start": v(-240.82, -719.84) * mm, "end": v(-225, -719.84) * mm});
            skLineSegment(sketch, "E294.MirrorCS", {"start": v(-85, -750) * mm, "end": v(-85, -760) * mm});
            skLineSegment(sketch, "E295.MirrorCS", {"start": v(-90.82, -719.84) * mm, "end": v(-75, -719.84) * mm});
            skLineSegment(sketch, "E296.MirrorCS", {"start": v(-215, -733.54) * mm, "end": v(-209.18, -733.54) * mm});
            skLineSegment(sketch, "E297.MirrorCS", {"start": v(65, -733.54) * mm, "end": v(59.18, -733.54) * mm});
            skLineSegment(sketch, "E298.MirrorCS", {"start": v(-85, -760) * mm, "end": v(-75, -760) * mm});
            skLineSegment(sketch, "E299.MirrorCS", {"start": v(65, -750) * mm, "end": v(65, -733.54) * mm});
            skLineSegment(sketch, "E300.MirrorCS", {"start": v(85, -750) * mm, "end": v(85, -733.54) * mm});
            skLineSegment(sketch, "E301.MirrorCS", {"start": v(-65, -750) * mm, "end": v(-65, -760) * mm});
            skLineSegment(sketch, "E302.MirrorCS", {"start": v(-65, -760) * mm, "end": v(-75, -760) * mm});
            skLineSegment(sketch, "E303.MirrorCS", {"start": v(235, -733.54) * mm, "end": v(240.82, -733.54) * mm});
            skLineSegment(sketch, "E304.MirrorCS", {"start": v(-65, -750) * mm, "end": v(-65, -733.54) * mm});
            skLineSegment(sketch, "E305.MirrorCS", {"start": v(-235, -760) * mm, "end": v(-225, -760) * mm});
            skLineSegment(sketch, "E306.MirrorCS", {"start": v(-215, -760) * mm, "end": v(-225, -760) * mm});
            skLineSegment(sketch, "E307.MirrorCS", {"start": v(65, -760) * mm, "end": v(75, -760) * mm});
            skLineSegment(sketch, "E308.MirrorCS", {"start": v(-209.18, -719.84) * mm, "end": v(-225, -719.84) * mm});
            skLineSegment(sketch, "E309.MirrorCS", {"start": v(65, -750) * mm, "end": v(65, -760) * mm});
            skLineSegment(sketch, "E310.MirrorCS", {"start": v(215, -760) * mm, "end": v(225, -760) * mm});
            skLineSegment(sketch, "E311.MirrorCS", {"start": v(90.82, -733.54) * mm, "end": v(90.82, -719.84) * mm});
            skLineSegment(sketch, "E312.MirrorCS", {"start": v(59.18, -733.54) * mm, "end": v(59.18, -719.84) * mm});
            skLineSegment(sketch, "E313.MirrorCS", {"start": v(-65, -733.54) * mm, "end": v(-59.18, -733.54) * mm});
            skLineSegment(sketch, "E314.MirrorCS", {"start": v(235, -760) * mm, "end": v(225, -760) * mm});
            skLineSegment(sketch, "E315.MirrorCS", {"start": v(90.82, -719.84) * mm, "end": v(75, -719.84) * mm});
            skLineSegment(sketch, "E316.MirrorCS", {"start": v(235, -750) * mm, "end": v(235, -733.54) * mm});
            skLineSegment(sketch, "E317.MirrorCS", {"start": v(85, -750) * mm, "end": v(85, -760) * mm});
            skLineSegment(sketch, "E318.MirrorCS", {"start": v(59.18, -719.84) * mm, "end": v(75, -719.84) * mm});
            skLineSegment(sketch, "E319.MirrorCS", {"start": v(235, -750) * mm, "end": v(235, -760) * mm});
            skLineSegment(sketch, "E320.MirrorCS", {"start": v(-209.18, -733.54) * mm, "end": v(-209.18, -719.84) * mm});
            skLineSegment(sketch, "E321.MirrorCS", {"start": v(240.82, -719.84) * mm, "end": v(225, -719.84) * mm});
            skLineSegment(sketch, "E322.MirrorCS", {"start": v(85, -760) * mm, "end": v(75, -760) * mm});
            skLineSegment(sketch, "E323.MirrorCS", {"start": v(-59.18, -719.84) * mm, "end": v(-75, -719.84) * mm});
            skLineSegment(sketch, "E324.MirrorCS", {"start": v(215, -750) * mm, "end": v(215, -760) * mm});
            skLineSegment(sketch, "E325.MirrorCS", {"start": v(209.18, -719.84) * mm, "end": v(225, -719.84) * mm});
            skLineSegment(sketch, "E326.MirrorCS", {"start": v(215, -733.54) * mm, "end": v(209.18, -733.54) * mm});
            skLineSegment(sketch, "E327.MirrorCS", {"start": v(209.18, -733.54) * mm, "end": v(209.18, -719.84) * mm});
            skLineSegment(sketch, "E328.MirrorCS", {"start": v(240.82, -733.54) * mm, "end": v(240.82, -719.84) * mm});
            skLineSegment(sketch, "E329.MirrorCS", {"start": v(215, -750) * mm, "end": v(215, -733.54) * mm});
            skLineSegment(sketch, "E330.MirrorCS", {"start": v(-59.18, -733.54) * mm, "end": v(-59.18, -719.84) * mm});
            skLineSegment(sketch, "E331.MirrorCS", {"start": v(-240.82, -719.84) * mm, "end": v(-90.82, -719.84) * mm, "construction": true});
            skLineSegment(sketch, "E332.MirrorCS", {"start": v(-225, -750) * mm, "end": v(-225, 750) * mm, "construction": true});
            skLineSegment(sketch, "E333.MirrorCS", {"start": v(75, -750) * mm, "end": v(75, 750) * mm, "construction": true});
            skLineSegment(sketch, "E334.MirrorCS", {"start": v(-75, -750) * mm, "end": v(-75, 750) * mm, "construction": true});
            skLineSegment(sketch, "E335.MirrorCS", {"start": v(225, -750) * mm, "end": v(225, 750) * mm, "construction": true});
            skSolve(sketch);
        }
        {
            var Q0;
            Q0 = qSketchRegion(id + "F6", true);
            extrude(context, id + "F7", {"entities" : qUnion([Q0]), "operationType" : NewBodyOperationType.REMOVE, "endBound" : BoundingType.SYMMETRIC, "oppositeDirection" : true, "depth" : 20000 * mm});
        }
        {
            var Q0;
            Q0=makeQuery(id+"F1.opExtrude","CAP_FACE",FACE,{"disambiguationData":[OSD([sQuery(id+"F0.wireOp",EDGE,"E0.bottom"),sQuery(id+"F0.wireOp",EDGE,"E0.top"),sQuery(id+"F0.wireOp",EDGE,"E0.left"),sQuery(id+"F0.wireOp",EDGE,"E0.right")])],"isStart":false});
            var sketch = newSketch(context, id + "F8", { "sketchPlane" : qUnion([Q0])});
            skLineSegment(sketch, "E336.bottom", {"start": v(-295, 670) * mm, "end": v(295, 670) * mm});
            skLineSegment(sketch, "E336.top", {"start": v(-295, -670) * mm, "end": v(295, -670) * mm});
            skLineSegment(sketch, "E336.left", {"start": v(-295, 670) * mm, "end": v(-295, -670) * mm});
            skLineSegment(sketch, "E336.right", {"start": v(295, 670) * mm, "end": v(295, -670) * mm});
            skPoint(sketch, "E336.middle", {"position": v(0, 0) * mm});
            skSolve(sketch);
        }
        {
            var Q0;
            Q0 = qSketchRegion(id + "F8", true);
            extrude(context, id + "F9", {"entities" : qUnion([Q0]), "operationType" : NewBodyOperationType.REMOVE, "oppositeDirection" : true, "depth" : 520 * mm});
        }
    });
